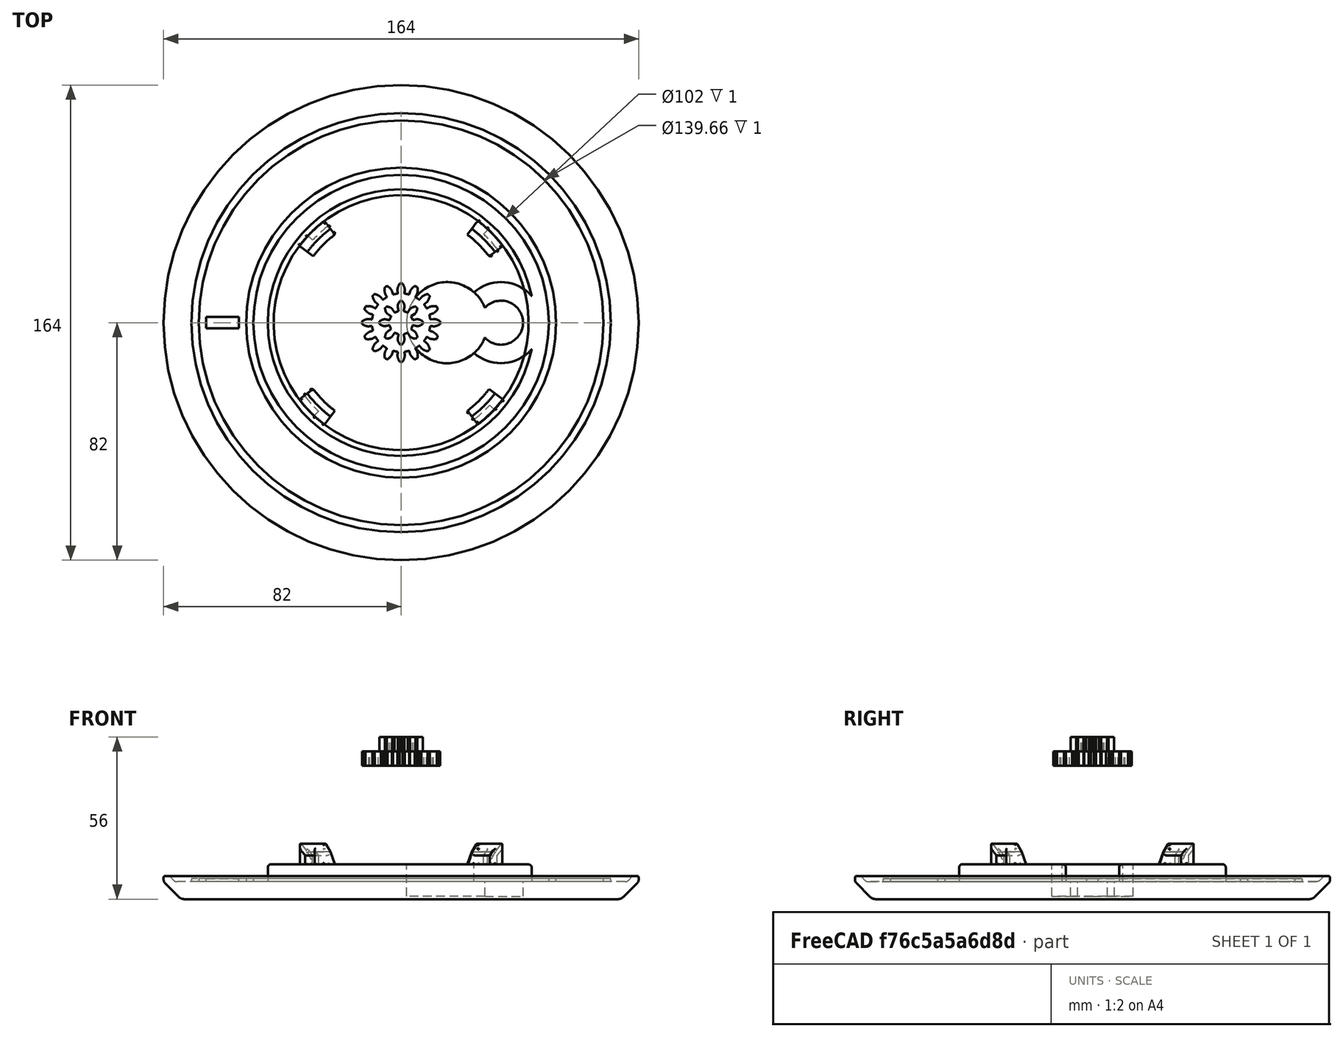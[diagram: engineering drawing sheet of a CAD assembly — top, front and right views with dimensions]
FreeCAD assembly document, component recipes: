
FREECAD ASSEMBLY — COMPONENT RECIPES ("smart_medication_box_v2")

This assembly document has 7 components, labeled P0..P6 below (a component is one placed body or linked part). 7 of them carry a construction recipe — the FreeCAD feature program that regenerates the part from scratch, quoted from this document or its linked companion documents; the rest are supplied as boundary geometry only. No exploded tour is included for this assembly.
COMPONENT P0 — recipe-attached ("base", modeled in this document).
Construction recipe (the document's own serialized feature program — sketch geometry with constraints, then the solid features built on it; lengths are millimeters unless a unit is written):

FEATURE [Sketcher::SketchObject] Sketch003
  ArcFitTolerance = 1e-06
  AttachmentSupport = -> [Origin006,XY_Plane003]
  FullyConstrained = true
  MakeInternals = true
  MapMode = 5
  expr: Constraints[0] = 104
  sketch-geometry (1):
    g0: Circle CenterX=0 CenterY=0 CenterZ=0 NormalX=0 NormalY=0 NormalZ=1 AngleXU=0 Radius=52
  constraints (2):
    c: Diameter(g0) = 104
    c: Coincident(g0,g-1)
FEATURE [PartDesign::Pad] Pad
  Direction = (0,0,1)
  Length = 6
  Length2 = 10
  Profile = -> Sketch003
  ReferenceAxis = -> Sketch003 [N_Axis]
  Refine = true
  Suppressed = false
  Type = 0
  expr: Length = 6
FEATURE [Sketcher::SketchObject] Sketch004
  ArcFitTolerance = 1e-06
  AttachmentSupport = -> [Pad]
  FullyConstrained = true
  MakeInternals = false
  MapMode = 5
  Placement = pos=(0,0,6) rot=(0,0,1;0rad)
  expr: Constraints[0] = 48 * 2 - 2
  sketch-geometry (1):
    g0: Circle CenterX=0 CenterY=0 CenterZ=0 NormalX=0 NormalY=0 NormalZ=1 AngleXU=0 Radius=47
  constraints (2):
    c: Diameter(g0) = 94
    c: Coincident(g0,g-1)
FEATURE [PartDesign::Pad] Pad001
  BaseFeature = -> Pad
  Direction = (0,0,1)
  Length = 6
  Length2 = 10
  Profile = -> Sketch004
  ReferenceAxis = -> Sketch004 [N_Axis]
  Refine = true
  Suppressed = false
  Type = 0
  expr: Length = 6
FEATURE [Sketcher::SketchObject] Sketch005
  ArcFitTolerance = 1e-06
  AttachmentSupport = -> [Pad001]
  ExternalGeometry = -> [Pad001]
  FullyConstrained = true
  MakeInternals = false
  MapMode = 5
  Placement = pos=(0,0,12) rot=(0,0,1;0rad)
  expr: Constraints[0] = 28
  expr: Constraints[4] = 11.5
  sketch-geometry (2):
    g0: Circle CenterX=35.5 CenterY=0 CenterZ=0 NormalX=0 NormalY=0 NormalZ=1 AngleXU=0 Radius=14
    g1: Circle [constr] CenterX=35.5 CenterY=0 CenterZ=0 NormalX=0 NormalY=0 NormalZ=1 AngleXU=0 Radius=11.5
  constraints (5):
    c: Diameter(g0) = 28
    c: Coincident(g1,g0)
    c: Tangent(g1,g-3)
    c: PointOnObject(g0,g-1)
    c: Distance(g0,g-3) = 11.5
FEATURE [PartDesign::Pocket] Pocket001
  BaseFeature = -> Pad001
  Direction = (0,0,-1)
  Length = 6
  Length2 = 5
  Profile = -> Sketch005
  ReferenceAxis = -> Sketch005 [N_Axis]
  Refine = true
  Suppressed = false
  Type = 0
  expr: Length = 6
FEATURE [Sketcher::SketchObject] Sketch006
  ArcFitTolerance = 1e-06
  AttachmentSupport = -> [Pocket001]
  ExternalGeometry = -> [Pocket001]
  FullyConstrained = true
  MakeInternals = false
  MapMode = 5
  Placement = pos=(0,0,6) rot=(0,0,1;0rad)
  sketch-geometry (1):
    g0: Circle CenterX=35.5 CenterY=0 CenterZ=0 NormalX=0 NormalY=0 NormalZ=1 AngleXU=0 Radius=7.6
  constraints (2):
    c: Diameter(g0) = 15.2
    c: Coincident(g0,g-4)
FEATURE [PartDesign::Pocket] Pocket002
  BaseFeature = -> Pocket001
  Direction = (0,0,-1)
  Length = 5
  Length2 = 5
  Profile = -> Sketch006
  ReferenceAxis = -> Sketch006 [N_Axis]
  Refine = true
  Suppressed = false
  Type = 0
FEATURE [Sketcher::SketchObject] Sketch007
  ArcFitTolerance = 1e-06
  AttachmentSupport = -> [Pocket002]
  ExternalGeometry = -> [Pocket002]
  FullyConstrained = true
  MakeInternals = false
  MapMode = 5
  Placement = pos=(0,0,12) rot=(0,0,1;0rad)
  expr: Constraints[0] = 28
  expr: Constraints[2] = -3
  sketch-geometry (1):
    g0: Circle CenterX=16.9 CenterY=0 CenterZ=0 NormalX=0 NormalY=0 NormalZ=1 AngleXU=0 Radius=14
  constraints (3):
    c: Diameter(g0) = 28
    c: PointOnObject(g0,g-1)
    c: Distance(g0,g-3) = -3
FEATURE [PartDesign::Pocket] Pocket003
  BaseFeature = -> Pocket002
  Direction = (0,0,-1)
  Length = 11
  Length2 = 5
  Profile = -> Sketch007
  ReferenceAxis = -> Sketch007 [N_Axis]
  Refine = true
  Suppressed = false
  Type = 0
  expr: Length = 11
FEATURE [Sketcher::SketchObject] Sketch009
  ArcFitTolerance = 1e-06
  FullyConstrained = true
  MakeInternals = false
  MapMode = 5
  Placement = pos=(53,0,0) rot=(1,0,0;1.5708rad)
  expr: Constraints[10] = 2
  expr: Constraints[3] = 22
  sketch-geometry (17):
    g0: LineSegment StartX=0 StartY=0 StartZ=0 EndX=0 EndY=3 EndZ=0
    g1: LineSegment StartX=0 StartY=3 StartZ=0 EndX=21.1716 EndY=3 EndZ=0
    g2: LineSegment StartX=22.5858 StartY=3.58579 StartZ=0 EndX=23.7071 EndY=4.70711 EndZ=0
    g3: LineSegment StartX=24.4142 StartY=5 StartZ=0 EndX=25.4142 EndY=5 EndZ=0
    g4: LineSegment StartX=26.4142 StartY=4 StartZ=0 EndX=26.4142 EndY=3.82843 EndZ=0
    g5: LineSegment StartX=25.8284 StartY=2.41421 StartZ=0 EndX=24 EndY=0.585786 EndZ=0
    g6: LineSegment StartX=0 StartY=0 StartZ=0 EndX=22.5858 EndY=0 EndZ=0
    g7: ArcOfCircle CenterX=25.4142 CenterY=4 CenterZ=0 NormalX=0 NormalY=0 NormalZ=1 AngleXU=0 Radius=1 StartAngle=0 EndAngle=1.5708
    g8: GeomPoint [constr] X=26.4142 Y=5 Z=0
    g9: ArcOfCircle CenterX=24.4142 CenterY=4 CenterZ=0 NormalX=0 NormalY=0 NormalZ=1 AngleXU=0 Radius=1 StartAngle=1.5708 EndAngle=2.35619
    g10: GeomPoint [constr] X=24 Y=5 Z=0
    g11: ArcOfCircle CenterX=24.4142 CenterY=3.82843 CenterZ=0 NormalX=0 NormalY=0 NormalZ=1 AngleXU=0 Radius=2 StartAngle=5.49779 EndAngle=6.28319
    g12: GeomPoint [constr] X=26.4142 Y=3 Z=0
    g13: ArcOfCircle CenterX=21.1716 CenterY=5 CenterZ=0 NormalX=0 NormalY=0 NormalZ=1 AngleXU=0 Radius=2 StartAngle=4.71239 EndAngle=5.49779
    g14: GeomPoint [constr] X=22 Y=3 Z=0
    g15: ArcOfCircle CenterX=22.5858 CenterY=2 CenterZ=0 NormalX=0 NormalY=0 NormalZ=1 AngleXU=0 Radius=2 StartAngle=4.71239 EndAngle=5.49779
    g16: GeomPoint [constr] X=23.4142 Y=0 Z=0
  constraints (40):
    c: Coincident(g-1,g0)
    c: Coincident(g0,g1)
    c: PointOnObject(g0,g-2)
    c: DistanceX(g1,g14) = 22
    c: PointOnObject(g16,g-1)
    c: Coincident(g6,g0)
    c: Parallel(g1,g6)
    c: Parallel(g3,g1)
    c: Perpendicular(g3,g4)
    c: PointOnObject(g12,g1)
    c: DistanceY(g12,g8) = 2
    c: PointOnObject(g8,g3)
    c: PointOnObject(g8,g4)
    c: Tangent(g3,g7) = 1.5708
    c: Tangent(g4,g7) = 1.5708
    c: PointOnObject(g10,g2)
    c: PointOnObject(g10,g3)
    c: Tangent(g2,g9) = 1.5708
    c: Tangent(g3,g9) = 1.5708
    c: PointOnObject(g12,g5)
    c: PointOnObject(g12,g4)
    c: Tangent(g5,g11) = 1.5708
    c: Tangent(g4,g11) = 1.5708
    c: PointOnObject(g14,g2)
    c: PointOnObject(g14,g1)
    c: Tangent(g2,g13) = -1.5708
    c: Tangent(g1,g13) = -1.5708
    c: PointOnObject(g16,g5)
    c: PointOnObject(g16,g6)
    c: Tangent(g5,g15) = 1.5708
    c: Tangent(g6,g15) = -1.5708
    c: Equal(g9,g7)
    c: Equal(g13,g11)
    c: Equal(g11,g15)
    c: Radius(g9) = 1
    c: Radius(g13) = 2
    c: Parallel(g5,g2)
    c: Angle(g-1,g5) = 0.785398
    c: DistanceY(g0,g0) = 3
    c: Distance(g3,g3) = 1
FEATURE [PartDesign::Revolution] Revolution
  Angle = 360
  Angle2 = 60
  Axis = (1e-16,1e-16,1)
  Base = (0,0,0)
  BaseFeature = -> Pocket003
  Profile = -> Sketch009
  ReferenceAxis = -> Z_Axis003
  Refine = true
  Reversed = true
  Suppressed = false
  Type = 0
FEATURE [PartDesign::Fillet] Fillet
  Base = -> Revolution [Edge30]
  BaseFeature = -> Revolution
  Radius = 1
  Refine = true
  SupportTransform = false
  Suppressed = false
  UseAllEdges = false
FEATURE [Sketcher::SketchObject] Sketch019
  ArcFitTolerance = 1e-06
  AttachmentSupport = -> [Fillet]
  FullyConstrained = true
  MakeInternals = false
  MapMode = 5
  Placement = pos=(0,0,12) rot=(0,0,1;0rad)
  sketch-geometry (1):
    g0: Circle CenterX=0 CenterY=0 CenterZ=0 NormalX=0 NormalY=0 NormalZ=1 AngleXU=0 Radius=44
  constraints (2):
    c: Diameter(g0) = 88
    c: Coincident(g0,g-1)
FEATURE [Sketcher::SketchObject] Sketch020
  ArcFitTolerance = 1e-06
  FullyConstrained = true
  MakeInternals = false
  MapMode = 5
  Placement = pos=(44,0,12) rot=(1,0,0;1.5708rad)
  sketch-geometry (9):
    g0: LineSegment StartX=-2.19203 StartY=0 StartZ=0 EndX=-2.19203 EndY=3.1 EndZ=0
    g1: LineSegment StartX=-2.19203 StartY=3.1 StartZ=0 EndX=0 EndY=5.29203 EndZ=0
    g2: LineSegment StartX=0 StartY=5.29203 StartZ=0 EndX=0 EndY=7.79203 EndZ=0
    g3: LineSegment StartX=-5.9535 StartY=0 StartZ=0 EndX=-2.19203 EndY=0 EndZ=0
    g4: LineSegment StartX=0 StartY=7.79203 StartZ=0 EndX=-3.44203 EndY=4.35 EndZ=0
    g5: LineSegment StartX=-3.44203 StartY=4.35 StartZ=0 EndX=-5.9535 EndY=0 EndZ=0
    g6: LineSegment [constr] StartX=-3.44203 StartY=4.35 StartZ=0 EndX=-2.19203 EndY=3.1 EndZ=0
    g7: LineSegment StartX=-2.19203 StartY=0 StartZ=0 EndX=0 EndY=0 EndZ=0
    g8: LineSegment StartX=0 StartY=0 StartZ=0 EndX=0 EndY=5.29203 EndZ=0
  constraints (24):
    c: PointOnObject(g0,g-1)
    c: Vertical(g0)
    c: Coincident(g0,g1)
    c: PointOnObject(g1,g-2)
    c: Coincident(g1,g2)
    c: Coincident(g3,g0)
    c: PointOnObject(g3,g-1)
    c: PointOnObject(g2,g-2)
    c: Angle(g1,g0) = 0.785398
    c: DistanceY(g0,g0) = 3.1
    c: Equal(g1,g0)
    c: DistanceY(g2,g2) = 2.5
    c: Coincident(g2,g4)
    c: Coincident(g4,g5)
    c: Coincident(g3,g5)
    c: Angle(g3,g5) = 1.0472
    c: Parallel(g4,g1)
    c: Coincident(g6,g4)
    c: Coincident(g6,g0)
    c: Perpendicular(g4,g6)
    c: Coincident(g7,g0)
    c: Coincident(g7,g-1)
    c: Coincident(g8,g7)
    c: Coincident(g8,g1)
FEATURE [PartDesign::Revolution] Revolution005
  Angle = 323
  Angle2 = 47
  Axis = (1e-16,1e-16,1)
  Base = (0,0,0)
  BaseFeature = -> Fillet
  Profile = -> Sketch020 [Edge4,Edge5,Edge2,Edge1,Edge3,Edge6]
  ReferenceAxis = -> Z_Axis003
  Refine = true
  Reversed = true
  Suppressed = false
  Type = 4
  expr: Angle = 323
  expr: Angle2 = 47
FEATURE [PartDesign::Revolution] Revolution006
  Angle = 313
  Angle2 = 53
  Axis = (1e-16,1e-16,1)
  Base = (0,0,0)
  BaseFeature = -> Revolution005
  Profile = -> Sketch020 [Edge8,Edge3,Edge4,Edge5,Edge6,Edge7]
  ReferenceAxis = -> Z_Axis003
  Refine = true
  Reversed = true
  Suppressed = false
  Type = 4
  expr: Angle = 313
  expr: Angle2 = 53
FEATURE [PartDesign::PolarPattern] PolarPattern004
  Angle = 360
  Axis = -> Z_Axis003
  BaseFeature = -> Revolution006
  Mode = 0
  Occurrences = 4
  Offset = 120
  Originals = -> [Revolution005,Revolution006]
  Refine = true
  Suppressed = false
  TransformMode = 0
  expr: Occurrences = 4
FEATURE [PartDesign::Fillet] Fillet005
  Base = -> PolarPattern004 [Face5]
  BaseFeature = -> PolarPattern004
  Radius = 0.5
  Refine = true
  SupportTransform = false
  Suppressed = false
  UseAllEdges = false
  expr: Radius = 0.5
FEATURE [PartDesign::Fillet] Fillet006
  Base = -> Fillet005 [?Face21,Face20]
  BaseFeature = -> Fillet005
  Radius = 0.5
  Refine = true
  SupportTransform = false
  Suppressed = false
  UseAllEdges = false
  expr: Radius = 0.5
FEATURE [PartDesign::Fillet] Fillet007
  Base = -> Fillet006 [Face29,Face32]
  BaseFeature = -> Fillet006
  Radius = 0.5
  Refine = true
  SupportTransform = false
  Suppressed = false
  UseAllEdges = false
FEATURE [PartDesign::Fillet] Fillet008
  Base = -> Fillet007 [Face44,Face41]
  BaseFeature = -> Fillet007
  Radius = 0.5
  Refine = true
  SupportTransform = false
  Suppressed = false
  UseAllEdges = false
FEATURE [Sketcher::SketchObject] Sketch027
  ArcFitTolerance = 1e-06
  AttachmentSupport = -> [Fillet008]
  ExternalGeometry = -> [Fillet008]
  FullyConstrained = true
  MakeInternals = false
  MapMode = 5
  Placement = pos=(7e-16,7e-16,6) rot=(0,0,1;0rad)
  expr: Constraints[7] = 1
  sketch-geometry (4):
    g0: Circle CenterX=0 CenterY=0 CenterZ=0 NormalX=0 NormalY=0 NormalZ=1 AngleXU=0 Radius=51
    g1: Circle CenterX=0 CenterY=0 CenterZ=0 NormalX=0 NormalY=0 NormalZ=1 AngleXU=0 Radius=76.3276
    g2: Circle CenterX=0 CenterY=0 CenterZ=0 NormalX=0 NormalY=0 NormalZ=1 AngleXU=0 Radius=73.8276
    g3: Circle CenterX=0 CenterY=0 CenterZ=0 NormalX=0 NormalY=0 NormalZ=1 AngleXU=0 Radius=68.8276
  constraints (11):
    c: PointOnObject(g0,g-1)
    c: PointOnObject(g0,g-2)
    c: Distance(g0,g-3) = 5
    c: PointOnObject(g1,g-1)
    c: PointOnObject(g2,g-1)
    c: PointOnObject(g2,g-2)
    c: PointOnObject(g1,g-2)
    c: Distance(g1,g-4) = 1
    c: Distance(g1,g2) = 2.5
    c: Coincident(g3,g0)
    c: Distance(g2,g3) = 5
FEATURE [PartDesign::Body] Body003
  AllowCompound = false
  Group = -> [Sketch003,Pad,Sketch004,Pad001,Sketch005,Pocket001,Sketch006,Pocket002,Sketch007,Pocket003,Sketch009,Revolution,Fillet,Sketch019,Sketch020,Revolution005,Revolution006,PolarPattern004,Fillet005,Fillet006,Fillet007,Fillet008,Sketch027]
  Origin = -> Origin006
  Tip = -> Fillet008
COMPONENT P1 — recipe-attached ("middle_gear", modeled in this document).
Construction recipe (the document's own serialized feature program — sketch geometry with constraints, then the solid features built on it; lengths are millimeters unless a unit is written):

FEATURE [PartDesign::Boolean] Boolean
  Group = -> [InvoluteGear003,InvoluteGear002,Body017]
  Refine = true
  Suppressed = false
  Type = 0
  UsePlacement = true
FEATURE [PartDesign::Fillet] Fillet001
  Base = -> Boolean [Face4]
  BaseFeature = -> Boolean
  Radius = 0.25
  Refine = true
  SupportTransform = false
  Suppressed = false
  UseAllEdges = false
  expr: Radius = 0.25
FEATURE [PartDesign::Fillet] Fillet002
  Base = -> Fillet001 [Face4,Face243]
  BaseFeature = -> Fillet001
  Radius = 0.2
  Refine = true
  SupportTransform = false
  Suppressed = false
  UseAllEdges = false
  expr: Radius = 0.2
FEATURE [PartDesign::Body] Body018
  AllowCompound = false
  Group = -> [Boolean,Fillet001,Fillet002]
  Origin = -> Origin030
  Tip = -> Fillet002
COMPONENT P2 — recipe-attached ("cover", modeled in this document).
Construction recipe (the document's own serialized feature program — sketch geometry with constraints, then the solid features built on it; lengths are millimeters unless a unit is written):

FEATURE [Sketcher::SketchObject] Sketch024
  ArcFitTolerance = 1e-06
  AttachmentSupport = -> [Origin040]
  FullyConstrained = true
  MakeInternals = false
  MapMode = 5
  sketch-geometry (5):
    g0: ArcOfCircle CenterX=0 CenterY=0 CenterZ=0 NormalX=0 NormalY=0 NormalZ=1 AngleXU=0 Radius=100 StartAngle=4.71239 EndAngle=10.7992
    g1: ArcOfCircle CenterX=0 CenterY=0 CenterZ=0 NormalX=0 NormalY=0 NormalZ=1 AngleXU=0 Radius=41 StartAngle=4.51604 EndAngle=4.71239
    g2: Circle CenterX=0 CenterY=0 CenterZ=0 NormalX=0 NormalY=0 NormalZ=1 AngleXU=0 Radius=38
    g3: LineSegment StartX=-7.5e-15 StartY=-41 StartZ=0 EndX=-1.84e-14 EndY=-100 EndZ=0
    g4: LineSegment StartX=-19.509 StartY=-98.0785 StartZ=0 EndX=-7.99869 EndY=-40.2122 EndZ=0
  constraints (14):
    c: Angle(g0) = 6.08684
    c: Coincident(g0,g-1)
    c: PointOnObject(g0,g-2)
    c: Coincident(g1,g0)
    c: PointOnObject(g1,g-2)
    c: Diameter(g2) = 76
    c: Coincident(g2,g0)
    c: Radius(g0) = 100
    c: Distance(g1,g2) = 3
    c: Coincident(g3,g1)
    c: Coincident(g3,g0)
    c: Coincident(g4,g0)
    c: Coincident(g4,g1)
    c: PointOnObject(g0,g4)
FEATURE [PartDesign::Pad] Pad008
  Direction = (0,0,1)
  Length = 1.5
  Length2 = 10
  Profile = -> Sketch024
  ReferenceAxis = -> Sketch024 [N_Axis]
  Refine = true
  Suppressed = false
  Type = 0
  expr: Length = 1.5
FEATURE [Sketcher::SketchObject] Sketch025
  ArcFitTolerance = 1e-06
  ExternalGeometry = -> [Pad008]
  FullyConstrained = false
  MakeInternals = false
  MapMode = 5
  Placement = pos=(-1.84e-14,-100,0) rot=(0.57735,-0.57735,-0.57735;2.0944rad)
  sketch-geometry (10):
    g0: LineSegment StartX=0 StartY=0 StartZ=0 EndX=0.693802 EndY=-1.2017 EndZ=0
    g1: LineSegment StartX=1.21047 StartY=-1.5 StartZ=0 EndX=2.01139 EndY=-1.5 EndZ=0
    g2: LineSegment StartX=2.37172 StartY=-0.875891 StartZ=0 EndX=1.18232 EndY=1.18422 EndZ=0
    g3: LineSegment StartX=0.63537 StartY=1.5 StartZ=0 EndX=0 EndY=1.5 EndZ=0
    g4: ArcOfCircle CenterX=0.63537 CenterY=0.868442 CenterZ=0 NormalX=0 NormalY=0 NormalZ=1 AngleXU=0 Radius=0.631558 StartAngle=0.523599 EndAngle=1.5708
    g5: GeomPoint [constr] X=1 Y=1.5 Z=0
    g6: ArcOfCircle CenterX=2.01139 CenterY=-1.08393 CenterZ=0 NormalX=0 NormalY=0 NormalZ=1 AngleXU=0 Radius=0.416073 StartAngle=4.71239 EndAngle=6.80678
    g7: GeomPoint [constr] X=2.73205 Y=-1.5 Z=0
    g8: ArcOfCircle CenterX=1.21047 CenterY=-0.903401 CenterZ=0 NormalX=0 NormalY=0 NormalZ=1 AngleXU=0 Radius=0.596599 StartAngle=3.66519 EndAngle=4.71239
    g9: GeomPoint [constr] X=0.866025 Y=-1.5 Z=0
  constraints (20):
    c: Coincident(g-3,g0)
    c: Coincident(g3,g-3)
    c: Horizontal(g3)
    c: Parallel(g0,g2)
    c: Parallel(g1,g3)
    c: Angle(g-2,g0) = 0.523599
    c: Distance(g5,g1) = 3
    c: DistanceX(g3,g5) = 1
    c: PointOnObject(g5,g3)
    c: PointOnObject(g5,g2)
    c: Tangent(g3,g4) = -1.5708
    c: Tangent(g2,g4) = -1.5708
    c: PointOnObject(g7,g2)
    c: PointOnObject(g7,g1)
    c: Tangent(g2,g6) = -1.5708
    c: Tangent(g1,g6) = -1.5708
    c: PointOnObject(g9,g1)
    c: PointOnObject(g9,g0)
    c: Tangent(g1,g8) = -1.5708
    c: Tangent(g0,g8) = -1.5708
FEATURE [PartDesign::Revolution] Revolution007
  Angle = 360
  Angle2 = 348.75
  Axis = (0,0,1)
  Base = (0,0,0)
  BaseFeature = -> Pad008
  Profile = -> Sketch025
  ReferenceAxis = -> Pad008 [Edge3]
  Refine = true
  Reversed = true
  Suppressed = false
  Type = 4
FEATURE [Sketcher::SketchObject] Sketch026
  ArcFitTolerance = 1e-06
  AttachmentSupport = -> [Revolution007]
  ExternalGeometry = -> [Revolution007]
  FullyConstrained = true
  MakeInternals = false
  MapMode = 5
  Placement = pos=(0,0,0) rot=(1,0,0;3.14159rad)
  sketch-geometry (1):
    g0: Circle CenterX=0 CenterY=0 CenterZ=0 NormalX=0 NormalY=0 NormalZ=1 AngleXU=0 Radius=41
  constraints (2):
    c: Coincident(g0,g-3)
    c: PointOnObject(g-4,g0)
FEATURE [PartDesign::Pad] Pad009
  BaseFeature = -> Revolution007
  Direction = (0,0,-1)
  Length = 3
  Length2 = 10
  Profile = -> Sketch026
  ReferenceAxis = -> Sketch026 [N_Axis]
  Refine = true
  Suppressed = false
  Type = 0
  expr: Length = 3
FEATURE [PartDesign::Chamfer] Chamfer001
  Angle = 45
  Base = -> Pad009 [Edge34]
  BaseFeature = -> Pad009
  ChamferType = 0
  FlipDirection = false
  Refine = true
  Size = 2
  Size2 = 1
  SupportTransform = false
  Suppressed = false
  UseAllEdges = false
  expr: Size = 2
FEATURE [PartDesign::Fillet] Fillet013
  Base = -> Chamfer001 [Edge1,Edge2,Edge24,Edge19]
  BaseFeature = -> Chamfer001
  Radius = 0.5
  Refine = true
  SupportTransform = false
  Suppressed = false
  UseAllEdges = false
  expr: Radius = 0.5
FEATURE [PartDesign::Body] Body023  label="cover"
  AllowCompound = false
  Group = -> [Sketch024,Pad008,Sketch025,Revolution007,Sketch026,Pad009,Chamfer001,Fillet013]
  Origin = -> Origin040
  Placement = pos=(-3.2e-15,-3.5e-15,43) rot=(0,0,-1;6.08242rad)
  Tip = -> Fillet013
COMPONENT P3 — recipe-attached ("desc_upper_ring", modeled in this document).
Construction recipe (the document's own serialized feature program — sketch geometry with constraints, then the solid features built on it; lengths are millimeters unless a unit is written):

FEATURE [Sketcher::SketchObject] Sketch021
  ArcFitTolerance = 1e-06
  AttachmentSupport = -> [Origin036]
  FullyConstrained = true
  MakeInternals = false
  MapMode = 5
  expr: Constraints[2] = 42.75 * 2
  expr: Constraints[3] = 51 * 2
  sketch-geometry (2):
    g0: Circle CenterX=0 CenterY=0 CenterZ=0 NormalX=0 NormalY=0 NormalZ=1 AngleXU=0 Radius=42.75
    g1: Circle CenterX=0 CenterY=0 CenterZ=0 NormalX=0 NormalY=0 NormalZ=1 AngleXU=0 Radius=51
  constraints (4):
    c: Coincident(g0,g-1)
    c: Coincident(g1,g0)
    c: Diameter(g0) = 85.5
    c: Diameter(g1) = 102
FEATURE [PartDesign::Pad] Pad006
  Direction = (0,0,1)
  Length = 3
  Length2 = 10
  Profile = -> Sketch021
  ReferenceAxis = -> Sketch021 [N_Axis]
  Refine = true
  Suppressed = false
  Type = 0
  expr: Length = 3
FEATURE [Sketcher::SketchObject] Sketch022
  ArcFitTolerance = 1e-06
  AttachmentSupport = -> [Pad006]
  FullyConstrained = false
  MakeInternals = false
  MapMode = 5
  Placement = pos=(0,0,3) rot=(0,0,1;0rad)
  sketch-geometry (4):
    g0: ArcOfCircle CenterX=0 CenterY=0 CenterZ=0 NormalX=0 NormalY=0 NormalZ=1 AngleXU=0 Radius=44.08 StartAngle=1.00282 EndAngle=1.41716
    g1: ArcOfCircle CenterX=0 CenterY=0 CenterZ=0 NormalX=0 NormalY=0 NormalZ=1 AngleXU=0 Radius=50.08 StartAngle=1.00282 EndAngle=1.41716
    g2: LineSegment StartX=6.74568 StartY=43.5608 StartZ=0 EndX=7.66388 EndY=49.4901 EndZ=0
    g3: LineSegment StartX=23.7119 StartY=37.159 StartZ=0 EndX=26.9394 EndY=42.217 EndZ=0
  constraints (11):
    c: Coincident(g1,g0)
    c: Coincident(g2,g0)
    c: Coincident(g2,g1)
    c: Coincident(g3,g0)
    c: Coincident(g3,g1)
    c: Equal(g2,g3)
    c: Perpendicular(g0,g2)
    c: Distance(g3,g3) = 6
    c: Radius(g0) = 44.08
    c: Angle(g0) = 0.414341
    c: Coincident(g0,g-1)
FEATURE [PartDesign::Pocket] Pocket006
  BaseFeature = -> Pad006
  Direction = (0,0,-1)
  Length = 1.5
  Length2 = 5
  Profile = -> Sketch022
  ReferenceAxis = -> Sketch022 [N_Axis]
  Refine = true
  Suppressed = false
  Type = 0
  expr: Length = 1.5
FEATURE [PartDesign::PolarPattern] PolarPattern005
  Angle = 360
  Axis = -> Sketch022 [N_Axis]
  BaseFeature = -> Pocket006
  Mode = 0
  Occurrences = 2
  Offset = 120
  Originals = -> [Pocket006]
  Refine = true
  Suppressed = false
  TransformMode = 0
FEATURE [PartDesign::Fillet] Fillet010
  Base = -> PolarPattern005 [Face2]
  BaseFeature = -> PolarPattern005
  Radius = 0.3
  Refine = true
  SupportTransform = false
  Suppressed = false
  UseAllEdges = false
  expr: Radius = 0.3
FEATURE [PartDesign::Fillet] Fillet011
  Base = -> Fillet010 [Face3]
  BaseFeature = -> Fillet010
  Radius = 0.4
  Refine = true
  SupportTransform = false
  Suppressed = false
  UseAllEdges = false
  expr: Radius = 0.4
FEATURE [Sketcher::SketchObject] Sketch023
  ArcFitTolerance = 1e-06
  AttachmentSupport = -> [Fillet011]
  FullyConstrained = false
  MakeInternals = false
  MapMode = 5
  Placement = pos=(0,0,0) rot=(1,0,0;3.14159rad)
  sketch-geometry (1190):
    g0: BSplineCurve PolesCount=2 KnotsCount=2 Degree=1 IsPeriodic=0
    g1: BSplineCurve PolesCount=2 KnotsCount=2 Degree=1 IsPeriodic=0
    g2: BSplineCurve PolesCount=2 KnotsCount=2 Degree=1 IsPeriodic=0
    g3: BSplineCurve PolesCount=2 KnotsCount=2 Degree=1 IsPeriodic=0
    g4: BSplineCurve PolesCount=2 KnotsCount=2 Degree=1 IsPeriodic=0
    g5: BSplineCurve PolesCount=2 KnotsCount=2 Degree=1 IsPeriodic=0
    g6: BSplineCurve PolesCount=2 KnotsCount=2 Degree=1 IsPeriodic=0
    g7: BSplineCurve PolesCount=2 KnotsCount=2 Degree=1 IsPeriodic=0
    g8: BSplineCurve PolesCount=2 KnotsCount=2 Degree=1 IsPeriodic=0
    g9: BSplineCurve PolesCount=2 KnotsCount=2 Degree=1 IsPeriodic=0
    g10: BSplineCurve PolesCount=2 KnotsCount=2 Degree=1 IsPeriodic=0
    g11: BSplineCurve PolesCount=2 KnotsCount=2 Degree=1 IsPeriodic=0
    g12: BSplineCurve PolesCount=2 KnotsCount=2 Degree=1 IsPeriodic=0
    g13: BSplineCurve PolesCount=2 KnotsCount=2 Degree=1 IsPeriodic=0
    g14: BSplineCurve PolesCount=2 KnotsCount=2 Degree=1 IsPeriodic=0
    g15: BSplineCurve PolesCount=2 KnotsCount=2 Degree=1 IsPeriodic=0
    g16: BSplineCurve PolesCount=2 KnotsCount=2 Degree=1 IsPeriodic=0
    g17: BSplineCurve PolesCount=2 KnotsCount=2 Degree=1 IsPeriodic=0
    g18: BSplineCurve PolesCount=2 KnotsCount=2 Degree=1 IsPeriodic=0
    g19: BSplineCurve PolesCount=2 KnotsCount=2 Degree=1 IsPeriodic=0
    g20: BSplineCurve PolesCount=2 KnotsCount=2 Degree=1 IsPeriodic=0
    g21: BSplineCurve PolesCount=2 KnotsCount=2 Degree=1 IsPeriodic=0
    g22: BSplineCurve PolesCount=2 KnotsCount=2 Degree=1 IsPeriodic=0
    g23: BSplineCurve PolesCount=2 KnotsCount=2 Degree=1 IsPeriodic=0
    g24: BSplineCurve PolesCount=2 KnotsCount=2 Degree=1 IsPeriodic=0
    g25: BSplineCurve PolesCount=2 KnotsCount=2 Degree=1 IsPeriodic=0
    g26: BSplineCurve PolesCount=2 KnotsCount=2 Degree=1 IsPeriodic=0
    g27: BSplineCurve PolesCount=2 KnotsCount=2 Degree=1 IsPeriodic=0
    g28: BSplineCurve PolesCount=2 KnotsCount=2 Degree=1 IsPeriodic=0
    g29: BSplineCurve PolesCount=2 KnotsCount=2 Degree=1 IsPeriodic=0
    g30: BSplineCurve PolesCount=2 KnotsCount=2 Degree=1 IsPeriodic=0
    g31: BSplineCurve PolesCount=2 KnotsCount=2 Degree=1 IsPeriodic=0
    g32: BSplineCurve PolesCount=2 KnotsCount=2 Degree=1 IsPeriodic=0
    g33: BSplineCurve PolesCount=2 KnotsCount=2 Degree=1 IsPeriodic=0
    g34: BSplineCurve PolesCount=2 KnotsCount=2 Degree=1 IsPeriodic=0
    g35: BSplineCurve PolesCount=2 KnotsCount=2 Degree=1 IsPeriodic=0
    g36: BSplineCurve PolesCount=2 KnotsCount=2 Degree=1 IsPeriodic=0
    g37: BSplineCurve PolesCount=2 KnotsCount=2 Degree=1 IsPeriodic=0
    g38: BSplineCurve PolesCount=2 KnotsCount=2 Degree=1 IsPeriodic=0
    g39: BSplineCurve PolesCount=2 KnotsCount=2 Degree=1 IsPeriodic=0
    g40: BSplineCurve PolesCount=2 KnotsCount=2 Degree=1 IsPeriodic=0
    g41: BSplineCurve PolesCount=2 KnotsCount=2 Degree=1 IsPeriodic=0
    g42: BSplineCurve PolesCount=2 KnotsCount=2 Degree=1 IsPeriodic=0
    g43: BSplineCurve PolesCount=2 KnotsCount=2 Degree=1 IsPeriodic=0
    g44: BSplineCurve PolesCount=2 KnotsCount=2 Degree=1 IsPeriodic=0
    g45: BSplineCurve PolesCount=2 KnotsCount=2 Degree=1 IsPeriodic=0
    g46: BSplineCurve PolesCount=2 KnotsCount=2 Degree=1 IsPeriodic=0
    g47: BSplineCurve PolesCount=2 KnotsCount=2 Degree=1 IsPeriodic=0
    g48: BSplineCurve PolesCount=2 KnotsCount=2 Degree=1 IsPeriodic=0
    g49: BSplineCurve PolesCount=2 KnotsCount=2 Degree=1 IsPeriodic=0
    g50: BSplineCurve PolesCount=2 KnotsCount=2 Degree=1 IsPeriodic=0
    g51: BSplineCurve PolesCount=2 KnotsCount=2 Degree=1 IsPeriodic=0
    g52: BSplineCurve PolesCount=2 KnotsCount=2 Degree=1 IsPeriodic=0
    g53: BSplineCurve PolesCount=2 KnotsCount=2 Degree=1 IsPeriodic=0
    g54: BSplineCurve PolesCount=2 KnotsCount=2 Degree=1 IsPeriodic=0
    g55: BSplineCurve PolesCount=2 KnotsCount=2 Degree=1 IsPeriodic=0
    g56: BSplineCurve PolesCount=2 KnotsCount=2 Degree=1 IsPeriodic=0
    g57: BSplineCurve PolesCount=2 KnotsCount=2 Degree=1 IsPeriodic=0
    g58: BSplineCurve PolesCount=2 KnotsCount=2 Degree=1 IsPeriodic=0
    g59: BSplineCurve PolesCount=2 KnotsCount=2 Degree=1 IsPeriodic=0
    g60: BSplineCurve PolesCount=2 KnotsCount=2 Degree=1 IsPeriodic=0
    g61: BSplineCurve PolesCount=2 KnotsCount=2 Degree=1 IsPeriodic=0
    g62: BSplineCurve PolesCount=2 KnotsCount=2 Degree=1 IsPeriodic=0
    g63: BSplineCurve PolesCount=2 KnotsCount=2 Degree=1 IsPeriodic=0
    g64: BSplineCurve PolesCount=2 KnotsCount=2 Degree=1 IsPeriodic=0
    g65: BSplineCurve PolesCount=2 KnotsCount=2 Degree=1 IsPeriodic=0
    g66: BSplineCurve PolesCount=2 KnotsCount=2 Degree=1 IsPeriodic=0
    g67: BSplineCurve PolesCount=2 KnotsCount=2 Degree=1 IsPeriodic=0
    g68: BSplineCurve PolesCount=2 KnotsCount=2 Degree=1 IsPeriodic=0
    g69: BSplineCurve PolesCount=2 KnotsCount=2 Degree=1 IsPeriodic=0
    g70: BSplineCurve PolesCount=2 KnotsCount=2 Degree=1 IsPeriodic=0
    g71: BSplineCurve PolesCount=2 KnotsCount=2 Degree=1 IsPeriodic=0
    g72: BSplineCurve PolesCount=2 KnotsCount=2 Degree=1 IsPeriodic=0
    g73: BSplineCurve PolesCount=2 KnotsCount=2 Degree=1 IsPeriodic=0
    g74: BSplineCurve PolesCount=2 KnotsCount=2 Degree=1 IsPeriodic=0
    g75: BSplineCurve PolesCount=2 KnotsCount=2 Degree=1 IsPeriodic=0
    g76: BSplineCurve PolesCount=2 KnotsCount=2 Degree=1 IsPeriodic=0
    g77: BSplineCurve PolesCount=2 KnotsCount=2 Degree=1 IsPeriodic=0
    g78: BSplineCurve PolesCount=2 KnotsCount=2 Degree=1 IsPeriodic=0
    g79: BSplineCurve PolesCount=2 KnotsCount=2 Degree=1 IsPeriodic=0
    g80: BSplineCurve PolesCount=2 KnotsCount=2 Degree=1 IsPeriodic=0
    g81: BSplineCurve PolesCount=2 KnotsCount=2 Degree=1 IsPeriodic=0
    g82: BSplineCurve PolesCount=2 KnotsCount=2 Degree=1 IsPeriodic=0
    g83: BSplineCurve PolesCount=2 KnotsCount=2 Degree=1 IsPeriodic=0
    g84: BSplineCurve PolesCount=2 KnotsCount=2 Degree=1 IsPeriodic=0
    g85: BSplineCurve PolesCount=2 KnotsCount=2 Degree=1 IsPeriodic=0
    g86: BSplineCurve PolesCount=2 KnotsCount=2 Degree=1 IsPeriodic=0
    g87: BSplineCurve PolesCount=2 KnotsCount=2 Degree=1 IsPeriodic=0
    g88: BSplineCurve PolesCount=2 KnotsCount=2 Degree=1 IsPeriodic=0
    g89: BSplineCurve PolesCount=2 KnotsCount=2 Degree=1 IsPeriodic=0
    g90: BSplineCurve PolesCount=2 KnotsCount=2 Degree=1 IsPeriodic=0
    g91: BSplineCurve PolesCount=2 KnotsCount=2 Degree=1 IsPeriodic=0
    g92: BSplineCurve PolesCount=2 KnotsCount=2 Degree=1 IsPeriodic=0
    g93: BSplineCurve PolesCount=2 KnotsCount=2 Degree=1 IsPeriodic=0
    g94: BSplineCurve PolesCount=2 KnotsCount=2 Degree=1 IsPeriodic=0
    g95: BSplineCurve PolesCount=2 KnotsCount=2 Degree=1 IsPeriodic=0
    g96: BSplineCurve PolesCount=2 KnotsCount=2 Degree=1 IsPeriodic=0
    g97: BSplineCurve PolesCount=2 KnotsCount=2 Degree=1 IsPeriodic=0
    g98: BSplineCurve PolesCount=2 KnotsCount=2 Degree=1 IsPeriodic=0
    g99: BSplineCurve PolesCount=2 KnotsCount=2 Degree=1 IsPeriodic=0
    g100: BSplineCurve PolesCount=2 KnotsCount=2 Degree=1 IsPeriodic=0
    g101: BSplineCurve PolesCount=2 KnotsCount=2 Degree=1 IsPeriodic=0
    g102: BSplineCurve PolesCount=2 KnotsCount=2 Degree=1 IsPeriodic=0
    g103: BSplineCurve PolesCount=2 KnotsCount=2 Degree=1 IsPeriodic=0
    g104: BSplineCurve PolesCount=2 KnotsCount=2 Degree=1 IsPeriodic=0
    g105: BSplineCurve PolesCount=2 KnotsCount=2 Degree=1 IsPeriodic=0
    g106: BSplineCurve PolesCount=2 KnotsCount=2 Degree=1 IsPeriodic=0
    g107: BSplineCurve PolesCount=2 KnotsCount=2 Degree=1 IsPeriodic=0
    g108: BSplineCurve PolesCount=2 KnotsCount=2 Degree=1 IsPeriodic=0
    g109: BSplineCurve PolesCount=2 KnotsCount=2 Degree=1 IsPeriodic=0
    g110: BSplineCurve PolesCount=2 KnotsCount=2 Degree=1 IsPeriodic=0
    g111: BSplineCurve PolesCount=2 KnotsCount=2 Degree=1 IsPeriodic=0
    g112: BSplineCurve PolesCount=2 KnotsCount=2 Degree=1 IsPeriodic=0
    g113: BSplineCurve PolesCount=2 KnotsCount=2 Degree=1 IsPeriodic=0
    g114: BSplineCurve PolesCount=2 KnotsCount=2 Degree=1 IsPeriodic=0
    g115: BSplineCurve PolesCount=2 KnotsCount=2 Degree=1 IsPeriodic=0
    g116: BSplineCurve PolesCount=2 KnotsCount=2 Degree=1 IsPeriodic=0
    g117: BSplineCurve PolesCount=2 KnotsCount=2 Degree=1 IsPeriodic=0
    g118: BSplineCurve PolesCount=2 KnotsCount=2 Degree=1 IsPeriodic=0
    g119: BSplineCurve PolesCount=2 KnotsCount=2 Degree=1 IsPeriodic=0
    g120: BSplineCurve PolesCount=2 KnotsCount=2 Degree=1 IsPeriodic=0
    g121: BSplineCurve PolesCount=2 KnotsCount=2 Degree=1 IsPeriodic=0
    g122: BSplineCurve PolesCount=2 KnotsCount=2 Degree=1 IsPeriodic=0
    g123: BSplineCurve PolesCount=2 KnotsCount=2 Degree=1 IsPeriodic=0
    g124: BSplineCurve PolesCount=2 KnotsCount=2 Degree=1 IsPeriodic=0
    g125: BSplineCurve PolesCount=2 KnotsCount=2 Degree=1 IsPeriodic=0
    g126: BSplineCurve PolesCount=2 KnotsCount=2 Degree=1 IsPeriodic=0
    g127: BSplineCurve PolesCount=2 KnotsCount=2 Degree=1 IsPeriodic=0
    g128: BSplineCurve PolesCount=3 KnotsCount=2 Degree=2 IsPeriodic=0
    g129: BSplineCurve PolesCount=3 KnotsCount=2 Degree=2 IsPeriodic=0
    g130: BSplineCurve PolesCount=3 KnotsCount=2 Degree=2 IsPeriodic=0
    g131: BSplineCurve PolesCount=3 KnotsCount=2 Degree=2 IsPeriodic=0
    g132: BSplineCurve PolesCount=3 KnotsCount=2 Degree=2 IsPeriodic=0
    g133: BSplineCurve PolesCount=3 KnotsCount=2 Degree=2 IsPeriodic=0
    g134: BSplineCurve PolesCount=3 KnotsCount=2 Degree=2 IsPeriodic=0
    g135: BSplineCurve PolesCount=3 KnotsCount=2 Degree=2 IsPeriodic=0
    g136: BSplineCurve PolesCount=3 KnotsCount=2 Degree=2 IsPeriodic=0
    g137: BSplineCurve PolesCount=3 KnotsCount=2 Degree=2 IsPeriodic=0
    g138: BSplineCurve PolesCount=3 KnotsCount=2 Degree=2 IsPeriodic=0
    g139: BSplineCurve PolesCount=3 KnotsCount=2 Degree=2 IsPeriodic=0
    g140: BSplineCurve PolesCount=3 KnotsCount=2 Degree=2 IsPeriodic=0
    g141: BSplineCurve PolesCount=3 KnotsCount=2 Degree=2 IsPeriodic=0
    g142: BSplineCurve PolesCount=3 KnotsCount=2 Degree=2 IsPeriodic=0
    g143: BSplineCurve PolesCount=3 KnotsCount=2 Degree=2 IsPeriodic=0
    g144: BSplineCurve PolesCount=2 KnotsCount=2 Degree=1 IsPeriodic=0
    g145: BSplineCurve PolesCount=2 KnotsCount=2 Degree=1 IsPeriodic=0
    g146: BSplineCurve PolesCount=2 KnotsCount=2 Degree=1 IsPeriodic=0
    g147: BSplineCurve PolesCount=2 KnotsCount=2 Degree=1 IsPeriodic=0
    g148: BSplineCurve PolesCount=2 KnotsCount=2 Degree=1 IsPeriodic=0
    g149: BSplineCurve PolesCount=2 KnotsCount=2 Degree=1 IsPeriodic=0
    g150: BSplineCurve PolesCount=2 KnotsCount=2 Degree=1 IsPeriodic=0
    g151: BSplineCurve PolesCount=2 KnotsCount=2 Degree=1 IsPeriodic=0
    g152: BSplineCurve PolesCount=2 KnotsCount=2 Degree=1 IsPeriodic=0
    g153: BSplineCurve PolesCount=2 KnotsCount=2 Degree=1 IsPeriodic=0
    g154: BSplineCurve PolesCount=2 KnotsCount=2 Degree=1 IsPeriodic=0
    g155: BSplineCurve PolesCount=2 KnotsCount=2 Degree=1 IsPeriodic=0
    g156: BSplineCurve PolesCount=3 KnotsCount=2 Degree=2 IsPeriodic=0
    g157: BSplineCurve PolesCount=3 KnotsCount=2 Degree=2 IsPeriodic=0
    g158: BSplineCurve PolesCount=3 KnotsCount=2 Degree=2 IsPeriodic=0
    g159: BSplineCurve PolesCount=3 KnotsCount=2 Degree=2 IsPeriodic=0
    g160: BSplineCurve PolesCount=3 KnotsCount=2 Degree=2 IsPeriodic=0
    g161: BSplineCurve PolesCount=3 KnotsCount=2 Degree=2 IsPeriodic=0
    g162: BSplineCurve PolesCount=3 KnotsCount=2 Degree=2 IsPeriodic=0
    g163: BSplineCurve PolesCount=3 KnotsCount=2 Degree=2 IsPeriodic=0
    g164: BSplineCurve PolesCount=3 KnotsCount=2 Degree=2 IsPeriodic=0
    g165: BSplineCurve PolesCount=3 KnotsCount=2 Degree=2 IsPeriodic=0
    g166: BSplineCurve PolesCount=2 KnotsCount=2 Degree=1 IsPeriodic=0
    g167: BSplineCurve PolesCount=3 KnotsCount=2 Degree=2 IsPeriodic=0
    g168: BSplineCurve PolesCount=3 KnotsCount=2 Degree=2 IsPeriodic=0
    g169: BSplineCurve PolesCount=3 KnotsCount=2 Degree=2 IsPeriodic=0
    g170: BSplineCurve PolesCount=3 KnotsCount=2 Degree=2 IsPeriodic=0
    g171: BSplineCurve PolesCount=3 KnotsCount=2 Degree=2 IsPeriodic=0
    g172: BSplineCurve PolesCount=3 KnotsCount=2 Degree=2 IsPeriodic=0
    g173: BSplineCurve PolesCount=3 KnotsCount=2 Degree=2 IsPeriodic=0
    g174: BSplineCurve PolesCount=3 KnotsCount=2 Degree=2 IsPeriodic=0
    g175: BSplineCurve PolesCount=3 KnotsCount=2 Degree=2 IsPeriodic=0
    g176: BSplineCurve PolesCount=2 KnotsCount=2 Degree=1 IsPeriodic=0
    g177: BSplineCurve PolesCount=2 KnotsCount=2 Degree=1 IsPeriodic=0
    g178: BSplineCurve PolesCount=2 KnotsCount=2 Degree=1 IsPeriodic=0
    g179: BSplineCurve PolesCount=3 KnotsCount=2 Degree=2 IsPeriodic=0
    g180: BSplineCurve PolesCount=3 KnotsCount=2 Degree=2 IsPeriodic=0
    g181: BSplineCurve PolesCount=3 KnotsCount=2 Degree=2 IsPeriodic=0
    g182: BSplineCurve PolesCount=3 KnotsCount=2 Degree=2 IsPeriodic=0
    g183: BSplineCurve PolesCount=2 KnotsCount=2 Degree=1 IsPeriodic=0
    g184: BSplineCurve PolesCount=3 KnotsCount=2 Degree=2 IsPeriodic=0
    g185: BSplineCurve PolesCount=3 KnotsCount=2 Degree=2 IsPeriodic=0
    g186: BSplineCurve PolesCount=3 KnotsCount=2 Degree=2 IsPeriodic=0
    g187: BSplineCurve PolesCount=3 KnotsCount=2 Degree=2 IsPeriodic=0
    g188: BSplineCurve PolesCount=3 KnotsCount=2 Degree=2 IsPeriodic=0
    g189: BSplineCurve PolesCount=2 KnotsCount=2 Degree=1 IsPeriodic=0
    g190: BSplineCurve PolesCount=2 KnotsCount=2 Degree=1 IsPeriodic=0
    g191: BSplineCurve PolesCount=2 KnotsCount=2 Degree=1 IsPeriodic=0
    g192: BSplineCurve PolesCount=3 KnotsCount=2 Degree=2 IsPeriodic=0
    g193: BSplineCurve PolesCount=3 KnotsCount=2 Degree=2 IsPeriodic=0
    g194: BSplineCurve PolesCount=3 KnotsCount=2 Degree=2 IsPeriodic=0
    g195: BSplineCurve PolesCount=3 KnotsCount=2 Degree=2 IsPeriodic=0
    g196: BSplineCurve PolesCount=3 KnotsCount=2 Degree=2 IsPeriodic=0
    g197: BSplineCurve PolesCount=3 KnotsCount=2 Degree=2 IsPeriodic=0
    g198: BSplineCurve PolesCount=2 KnotsCount=2 Degree=1 IsPeriodic=0
    g199: BSplineCurve PolesCount=3 KnotsCount=2 Degree=2 IsPeriodic=0
    g200: BSplineCurve PolesCount=3 KnotsCount=2 Degree=2 IsPeriodic=0
    g201: BSplineCurve PolesCount=3 KnotsCount=2 Degree=2 IsPeriodic=0
    g202: BSplineCurve PolesCount=3 KnotsCount=2 Degree=2 IsPeriodic=0
    g203: BSplineCurve PolesCount=3 KnotsCount=2 Degree=2 IsPeriodic=0
    g204: BSplineCurve PolesCount=3 KnotsCount=2 Degree=2 IsPeriodic=0
    g205: BSplineCurve PolesCount=2 KnotsCount=2 Degree=1 IsPeriodic=0
    g206: BSplineCurve PolesCount=3 KnotsCount=2 Degree=2 IsPeriodic=0
    g207: BSplineCurve PolesCount=3 KnotsCount=2 Degree=2 IsPeriodic=0
    g208: BSplineCurve PolesCount=2 KnotsCount=2 Degree=1 IsPeriodic=0
    g209: BSplineCurve PolesCount=2 KnotsCount=2 Degree=1 IsPeriodic=0
    g210: BSplineCurve PolesCount=2 KnotsCount=2 Degree=1 IsPeriodic=0
    g211: BSplineCurve PolesCount=2 KnotsCount=2 Degree=1 IsPeriodic=0
    g212: BSplineCurve PolesCount=2 KnotsCount=2 Degree=1 IsPeriodic=0
    g213: BSplineCurve PolesCount=2 KnotsCount=2 Degree=1 IsPeriodic=0
    g214: BSplineCurve PolesCount=2 KnotsCount=2 Degree=1 IsPeriodic=0
    g215: BSplineCurve PolesCount=2 KnotsCount=2 Degree=1 IsPeriodic=0
    g216: BSplineCurve PolesCount=2 KnotsCount=2 Degree=1 IsPeriodic=0
    g217: BSplineCurve PolesCount=2 KnotsCount=2 Degree=1 IsPeriodic=0
    g218: BSplineCurve PolesCount=2 KnotsCount=2 Degree=1 IsPeriodic=0
    g219: BSplineCurve PolesCount=2 KnotsCount=2 Degree=1 IsPeriodic=0
    g220: BSplineCurve PolesCount=2 KnotsCount=2 Degree=1 IsPeriodic=0
    g221: BSplineCurve PolesCount=2 KnotsCount=2 Degree=1 IsPeriodic=0
    g222: BSplineCurve PolesCount=2 KnotsCount=2 Degree=1 IsPeriodic=0
    g223: BSplineCurve PolesCount=2 KnotsCount=2 Degree=1 IsPeriodic=0
    g224: BSplineCurve PolesCount=3 KnotsCount=2 Degree=2 IsPeriodic=0
    g225: BSplineCurve PolesCount=3 KnotsCount=2 Degree=2 IsPeriodic=0
    g226: BSplineCurve PolesCount=3 KnotsCount=2 Degree=2 IsPeriodic=0
    g227: BSplineCurve PolesCount=3 KnotsCount=2 Degree=2 IsPeriodic=0
    g228: BSplineCurve PolesCount=3 KnotsCount=2 Degree=2 IsPeriodic=0
    g229: BSplineCurve PolesCount=3 KnotsCount=2 Degree=2 IsPeriodic=0
    g230: BSplineCurve PolesCount=2 KnotsCount=2 Degree=1 IsPeriodic=0
    g231: BSplineCurve PolesCount=3 KnotsCount=2 Degree=2 IsPeriodic=0
    g232: BSplineCurve PolesCount=3 KnotsCount=2 Degree=2 IsPeriodic=0
    g233: BSplineCurve PolesCount=3 KnotsCount=2 Degree=2 IsPeriodic=0
    g234: BSplineCurve PolesCount=3 KnotsCount=2 Degree=2 IsPeriodic=0
    g235: BSplineCurve PolesCount=3 KnotsCount=2 Degree=2 IsPeriodic=0
    g236: BSplineCurve PolesCount=3 KnotsCount=2 Degree=2 IsPeriodic=0
    g237: BSplineCurve PolesCount=3 KnotsCount=2 Degree=2 IsPeriodic=0
    g238: BSplineCurve PolesCount=2 KnotsCount=2 Degree=1 IsPeriodic=0
    g239: BSplineCurve PolesCount=2 KnotsCount=2 Degree=1 IsPeriodic=0
    g240: BSplineCurve PolesCount=2 KnotsCount=2 Degree=1 IsPeriodic=0
    g241: BSplineCurve PolesCount=2 KnotsCount=2 Degree=1 IsPeriodic=0
    g242: BSplineCurve PolesCount=2 KnotsCount=2 Degree=1 IsPeriodic=0
    g243: BSplineCurve PolesCount=2 KnotsCount=2 Degree=1 IsPeriodic=0
    g244: BSplineCurve PolesCount=3 KnotsCount=2 Degree=2 IsPeriodic=0
    g245: BSplineCurve PolesCount=3 KnotsCount=2 Degree=2 IsPeriodic=0
    g246: BSplineCurve PolesCount=3 KnotsCount=2 Degree=2 IsPeriodic=0
    g247: BSplineCurve PolesCount=3 KnotsCount=2 Degree=2 IsPeriodic=0
    g248: BSplineCurve PolesCount=3 KnotsCount=2 Degree=2 IsPeriodic=0
    g249: BSplineCurve PolesCount=3 KnotsCount=2 Degree=2 IsPeriodic=0
    g250: BSplineCurve PolesCount=3 KnotsCount=2 Degree=2 IsPeriodic=0
    g251: BSplineCurve PolesCount=3 KnotsCount=2 Degree=2 IsPeriodic=0
    g252: BSplineCurve PolesCount=3 KnotsCount=2 Degree=2 IsPeriodic=0
    g253: BSplineCurve PolesCount=3 KnotsCount=2 Degree=2 IsPeriodic=0
    g254: BSplineCurve PolesCount=3 KnotsCount=2 Degree=2 IsPeriodic=0
    g255: BSplineCurve PolesCount=3 KnotsCount=2 Degree=2 IsPeriodic=0
    g256: BSplineCurve PolesCount=3 KnotsCount=2 Degree=2 IsPeriodic=0
    g257: BSplineCurve PolesCount=3 KnotsCount=2 Degree=2 IsPeriodic=0
    g258: BSplineCurve PolesCount=3 KnotsCount=2 Degree=2 IsPeriodic=0
    g259: BSplineCurve PolesCount=3 KnotsCount=2 Degree=2 IsPeriodic=0
    g260: BSplineCurve PolesCount=3 KnotsCount=2 Degree=2 IsPeriodic=0
    g261: BSplineCurve PolesCount=2 KnotsCount=2 Degree=1 IsPeriodic=0
    g262: BSplineCurve PolesCount=3 KnotsCount=2 Degree=2 IsPeriodic=0
    g263: BSplineCurve PolesCount=3 KnotsCount=2 Degree=2 IsPeriodic=0
    g264: BSplineCurve PolesCount=3 KnotsCount=2 Degree=2 IsPeriodic=0
    g265: BSplineCurve PolesCount=3 KnotsCount=2 Degree=2 IsPeriodic=0
    g266: BSplineCurve PolesCount=3 KnotsCount=2 Degree=2 IsPeriodic=0
    g267: BSplineCurve PolesCount=3 KnotsCount=2 Degree=2 IsPeriodic=0
    g268: BSplineCurve PolesCount=3 KnotsCount=2 Degree=2 IsPeriodic=0
    g269: BSplineCurve PolesCount=3 KnotsCount=2 Degree=2 IsPeriodic=0
    g270: BSplineCurve PolesCount=3 KnotsCount=2 Degree=2 IsPeriodic=0
    g271: BSplineCurve PolesCount=3 KnotsCount=2 Degree=2 IsPeriodic=0
    g272: BSplineCurve PolesCount=3 KnotsCount=2 Degree=2 IsPeriodic=0
    g273: BSplineCurve PolesCount=2 KnotsCount=2 Degree=1 IsPeriodic=0
    g274: BSplineCurve PolesCount=3 KnotsCount=2 Degree=2 IsPeriodic=0
    g275: BSplineCurve PolesCount=3 KnotsCount=2 Degree=2 IsPeriodic=0
    g276: BSplineCurve PolesCount=2 KnotsCount=2 Degree=1 IsPeriodic=0
    g277: BSplineCurve PolesCount=2 KnotsCount=2 Degree=1 IsPeriodic=0
    g278: BSplineCurve PolesCount=2 KnotsCount=2 Degree=1 IsPeriodic=0
    g279: BSplineCurve PolesCount=2 KnotsCount=2 Degree=1 IsPeriodic=0
    g280: BSplineCurve PolesCount=3 KnotsCount=2 Degree=2 IsPeriodic=0
    g281: BSplineCurve PolesCount=3 KnotsCount=2 Degree=2 IsPeriodic=0
    g282: BSplineCurve PolesCount=3 KnotsCount=2 Degree=2 IsPeriodic=0
    g283: BSplineCurve PolesCount=3 KnotsCount=2 Degree=2 IsPeriodic=0
    g284: BSplineCurve PolesCount=3 KnotsCount=2 Degree=2 IsPeriodic=0
    g285: BSplineCurve PolesCount=2 KnotsCount=2 Degree=1 IsPeriodic=0
    g286: BSplineCurve PolesCount=3 KnotsCount=2 Degree=2 IsPeriodic=0
    g287: BSplineCurve PolesCount=3 KnotsCount=2 Degree=2 IsPeriodic=0
    g288: BSplineCurve PolesCount=3 KnotsCount=2 Degree=2 IsPeriodic=0
    g289: BSplineCurve PolesCount=3 KnotsCount=2 Degree=2 IsPeriodic=0
    g290: BSplineCurve PolesCount=3 KnotsCount=2 Degree=2 IsPeriodic=0
    g291: BSplineCurve PolesCount=3 KnotsCount=2 Degree=2 IsPeriodic=0
    g292: BSplineCurve PolesCount=2 KnotsCount=2 Degree=1 IsPeriodic=0
    g293: BSplineCurve PolesCount=3 KnotsCount=2 Degree=2 IsPeriodic=0
    g294: BSplineCurve PolesCount=3 KnotsCount=2 Degree=2 IsPeriodic=0
    g295: BSplineCurve PolesCount=3 KnotsCount=2 Degree=2 IsPeriodic=0
    g296: BSplineCurve PolesCount=3 KnotsCount=2 Degree=2 IsPeriodic=0
    g297: BSplineCurve PolesCount=3 KnotsCount=2 Degree=2 IsPeriodic=0
    g298: BSplineCurve PolesCount=3 KnotsCount=2 Degree=2 IsPeriodic=0
    g299: BSplineCurve PolesCount=3 KnotsCount=2 Degree=2 IsPeriodic=0
    g300: BSplineCurve PolesCount=3 KnotsCount=2 Degree=2 IsPeriodic=0
    g301: BSplineCurve PolesCount=3 KnotsCount=2 Degree=2 IsPeriodic=0
    g302: BSplineCurve PolesCount=3 KnotsCount=2 Degree=2 IsPeriodic=0
    g303: BSplineCurve PolesCount=3 KnotsCount=2 Degree=2 IsPeriodic=0
    g304: BSplineCurve PolesCount=3 KnotsCount=2 Degree=2 IsPeriodic=0
    g305: BSplineCurve PolesCount=3 KnotsCount=2 Degree=2 IsPeriodic=0
    g306: BSplineCurve PolesCount=3 KnotsCount=2 Degree=2 IsPeriodic=0
    g307: BSplineCurve PolesCount=3 KnotsCount=2 Degree=2 IsPeriodic=0
    g308: BSplineCurve PolesCount=3 KnotsCount=2 Degree=2 IsPeriodic=0
    g309: BSplineCurve PolesCount=3 KnotsCount=2 Degree=2 IsPeriodic=0
    g310: BSplineCurve PolesCount=3 KnotsCount=2 Degree=2 IsPeriodic=0
    g311: BSplineCurve PolesCount=3 KnotsCount=2 Degree=2 IsPeriodic=0
    g312: BSplineCurve PolesCount=3 KnotsCount=2 Degree=2 IsPeriodic=0
    g313: BSplineCurve PolesCount=3 KnotsCount=2 Degree=2 IsPeriodic=0
    g314: BSplineCurve PolesCount=3 KnotsCount=2 Degree=2 IsPeriodic=0
    g315: BSplineCurve PolesCount=3 KnotsCount=2 Degree=2 IsPeriodic=0
    g316: BSplineCurve PolesCount=3 KnotsCount=2 Degree=2 IsPeriodic=0
    g317: BSplineCurve PolesCount=3 KnotsCount=2 Degree=2 IsPeriodic=0
    g318: BSplineCurve PolesCount=3 KnotsCount=2 Degree=2 IsPeriodic=0
    g319: BSplineCurve PolesCount=3 KnotsCount=2 Degree=2 IsPeriodic=0
    g320: BSplineCurve PolesCount=2 KnotsCount=2 Degree=1 IsPeriodic=0
    g321: BSplineCurve PolesCount=3 KnotsCount=2 Degree=2 IsPeriodic=0
    g322: BSplineCurve PolesCount=3 KnotsCount=2 Degree=2 IsPeriodic=0
    g323: BSplineCurve PolesCount=3 KnotsCount=2 Degree=2 IsPeriodic=0
    g324: BSplineCurve PolesCount=3 KnotsCount=2 Degree=2 IsPeriodic=0
    g325: BSplineCurve PolesCount=3 KnotsCount=2 Degree=2 IsPeriodic=0
    g326: BSplineCurve PolesCount=3 KnotsCount=2 Degree=2 IsPeriodic=0
    g327: BSplineCurve PolesCount=3 KnotsCount=2 Degree=2 IsPeriodic=0
    g328: BSplineCurve PolesCount=3 KnotsCount=2 Degree=2 IsPeriodic=0
    g329: BSplineCurve PolesCount=3 KnotsCount=2 Degree=2 IsPeriodic=0
    g330: BSplineCurve PolesCount=3 KnotsCount=2 Degree=2 IsPeriodic=0
    g331: BSplineCurve PolesCount=3 KnotsCount=2 Degree=2 IsPeriodic=0
    g332: BSplineCurve PolesCount=3 KnotsCount=2 Degree=2 IsPeriodic=0
    g333: BSplineCurve PolesCount=3 KnotsCount=2 Degree=2 IsPeriodic=0
    g334: BSplineCurve PolesCount=3 KnotsCount=2 Degree=2 IsPeriodic=0
    g335: BSplineCurve PolesCount=3 KnotsCount=2 Degree=2 IsPeriodic=0
    g336: BSplineCurve PolesCount=3 KnotsCount=2 Degree=2 IsPeriodic=0
    g337: BSplineCurve PolesCount=2 KnotsCount=2 Degree=1 IsPeriodic=0
    g338: BSplineCurve PolesCount=2 KnotsCount=2 Degree=1 IsPeriodic=0
    g339: BSplineCurve PolesCount=2 KnotsCount=2 Degree=1 IsPeriodic=0
    g340: BSplineCurve PolesCount=2 KnotsCount=2 Degree=1 IsPeriodic=0
    g341: BSplineCurve PolesCount=2 KnotsCount=2 Degree=1 IsPeriodic=0
    g342: BSplineCurve PolesCount=2 KnotsCount=2 Degree=1 IsPeriodic=0
    g343: BSplineCurve PolesCount=2 KnotsCount=2 Degree=1 IsPeriodic=0
    g344: BSplineCurve PolesCount=2 KnotsCount=2 Degree=1 IsPeriodic=0
    g345: BSplineCurve PolesCount=2 KnotsCount=2 Degree=1 IsPeriodic=0
    g346: BSplineCurve PolesCount=2 KnotsCount=2 Degree=1 IsPeriodic=0
    g347: BSplineCurve PolesCount=2 KnotsCount=2 Degree=1 IsPeriodic=0
    g348: BSplineCurve PolesCount=3 KnotsCount=2 Degree=2 IsPeriodic=0
    g349: BSplineCurve PolesCount=3 KnotsCount=2 Degree=2 IsPeriodic=0
    g350: BSplineCurve PolesCount=3 KnotsCount=2 Degree=2 IsPeriodic=0
    g351: BSplineCurve PolesCount=3 KnotsCount=2 Degree=2 IsPeriodic=0
    g352: BSplineCurve PolesCount=3 KnotsCount=2 Degree=2 IsPeriodic=0
    g353: BSplineCurve PolesCount=3 KnotsCount=2 Degree=2 IsPeriodic=0
    g354: BSplineCurve PolesCount=3 KnotsCount=2 Degree=2 IsPeriodic=0
    g355: BSplineCurve PolesCount=3 KnotsCount=2 Degree=2 IsPeriodic=0
    g356: BSplineCurve PolesCount=3 KnotsCount=2 Degree=2 IsPeriodic=0
    g357: BSplineCurve PolesCount=3 KnotsCount=2 Degree=2 IsPeriodic=0
    g358: BSplineCurve PolesCount=3 KnotsCount=2 Degree=2 IsPeriodic=0
    g359: BSplineCurve PolesCount=3 KnotsCount=2 Degree=2 IsPeriodic=0
    g360: BSplineCurve PolesCount=3 KnotsCount=2 Degree=2 IsPeriodic=0
    g361: BSplineCurve PolesCount=3 KnotsCount=2 Degree=2 IsPeriodic=0
    g362: BSplineCurve PolesCount=3 KnotsCount=2 Degree=2 IsPeriodic=0
    g363: BSplineCurve PolesCount=3 KnotsCount=2 Degree=2 IsPeriodic=0
    g364: BSplineCurve PolesCount=2 KnotsCount=2 Degree=1 IsPeriodic=0
    g365: BSplineCurve PolesCount=2 KnotsCount=2 Degree=1 IsPeriodic=0
    g366: BSplineCurve PolesCount=2 KnotsCount=2 Degree=1 IsPeriodic=0
    g367: BSplineCurve PolesCount=2 KnotsCount=2 Degree=1 IsPeriodic=0
    g368: BSplineCurve PolesCount=2 KnotsCount=2 Degree=1 IsPeriodic=0
    g369: BSplineCurve PolesCount=2 KnotsCount=2 Degree=1 IsPeriodic=0
    g370: BSplineCurve PolesCount=2 KnotsCount=2 Degree=1 IsPeriodic=0
    g371: BSplineCurve PolesCount=2 KnotsCount=2 Degree=1 IsPeriodic=0
    g372: BSplineCurve PolesCount=2 KnotsCount=2 Degree=1 IsPeriodic=0
    g373: BSplineCurve PolesCount=2 KnotsCount=2 Degree=1 IsPeriodic=0
    g374: BSplineCurve PolesCount=2 KnotsCount=2 Degree=1 IsPeriodic=0
    g375: BSplineCurve PolesCount=2 KnotsCount=2 Degree=1 IsPeriodic=0
    g376: BSplineCurve PolesCount=2 KnotsCount=2 Degree=1 IsPeriodic=0
    g377: BSplineCurve PolesCount=2 KnotsCount=2 Degree=1 IsPeriodic=0
    g378: BSplineCurve PolesCount=2 KnotsCount=2 Degree=1 IsPeriodic=0
    g379: BSplineCurve PolesCount=2 KnotsCount=2 Degree=1 IsPeriodic=0
    g380: BSplineCurve PolesCount=2 KnotsCount=2 Degree=1 IsPeriodic=0
    g381: BSplineCurve PolesCount=2 KnotsCount=2 Degree=1 IsPeriodic=0
    g382: BSplineCurve PolesCount=2 KnotsCount=2 Degree=1 IsPeriodic=0
    g383: BSplineCurve PolesCount=2 KnotsCount=2 Degree=1 IsPeriodic=0
    g384: BSplineCurve PolesCount=2 KnotsCount=2 Degree=1 IsPeriodic=0
    g385: BSplineCurve PolesCount=2 KnotsCount=2 Degree=1 IsPeriodic=0
    g386: BSplineCurve PolesCount=2 KnotsCount=2 Degree=1 IsPeriodic=0
    g387: BSplineCurve PolesCount=2 KnotsCount=2 Degree=1 IsPeriodic=0
    g388: BSplineCurve PolesCount=2 KnotsCount=2 Degree=1 IsPeriodic=0
    g389: BSplineCurve PolesCount=2 KnotsCount=2 Degree=1 IsPeriodic=0
    g390: BSplineCurve PolesCount=2 KnotsCount=2 Degree=1 IsPeriodic=0
    g391: BSplineCurve PolesCount=2 KnotsCount=2 Degree=1 IsPeriodic=0
    g392: BSplineCurve PolesCount=2 KnotsCount=2 Degree=1 IsPeriodic=0
    g393: BSplineCurve PolesCount=2 KnotsCount=2 Degree=1 IsPeriodic=0
    g394: BSplineCurve PolesCount=2 KnotsCount=2 Degree=1 IsPeriodic=0
    g395: BSplineCurve PolesCount=2 KnotsCount=2 Degree=1 IsPeriodic=0
    g396: BSplineCurve PolesCount=2 KnotsCount=2 Degree=1 IsPeriodic=0
    g397: BSplineCurve PolesCount=2 KnotsCount=2 Degree=1 IsPeriodic=0
    g398: BSplineCurve PolesCount=3 KnotsCount=2 Degree=2 IsPeriodic=0
    g399: BSplineCurve PolesCount=3 KnotsCount=2 Degree=2 IsPeriodic=0
    ... +790 more geometry lines
  constraints (1190):
    c: Coincident(g93,g94)
    c: Coincident(g92,g93)
    c: Coincident(g282,g284)
    c: Coincident(g273,g274)
    c: Coincident(g272,g273)
    c: Coincident(g280,g282)
    c: Coincident(g88,g89)
    c: Coincident(g96,g97)
    c: Coincident(g299,g300)
    c: Coincident(g284,g286)
    c: Coincident(g298,g299)
    c: Coincident(g96,g99)
    c: Coincident(g89,g90)
    c: Coincident(g280,g281)
    c: Coincident(g271,g272)
    c: Coincident(g298,g304)
    c: Coincident(g300,g301)
    c: Coincident(g286,g288)
    c: Coincident(g274,g275)
    c: Coincident(g281,g283)
    c: Coincident(g303,g304)
    c: Coincident(g301,g302)
    c: Coincident(g288,g290)
    c: Coincident(g302,g303)
    c: Coincident(g283,g285)
    c: Coincident(g285,g287)
    c: Coincident(g290,g292)
    c: Coincident(g292,g294)
    c: Coincident(g270,g271)
    c: Coincident(g306,g308)
    c: Coincident(g287,g289)
    c: Coincident(g249,g251)
    c: Coincident(g314,g316)
    c: Coincident(g305,g306)
    c: Coincident(g308,g310)
    c: Coincident(g294,g296)
    c: Coincident(g251,g253)
    c: Coincident(g312,g314)
    c: Coincident(g263,g264)
    c: Coincident(g322,g324)
    c: Coincident(g316,g318)
    c: Coincident(g264,g265)
    c: Coincident(g289,g291)
    c: Coincident(g305,g307)
    c: Coincident(g324,g326)
    c: Coincident(g247,g249)
    c: Coincident(g310,g311)
    c: Coincident(g296,g297)
    c: Coincident(g262,g263)
    c: Coincident(g276,g277)
    c: Coincident(g320,g322)
    c: Coincident(g318,g320)
    c: Coincident(g265,g266)
    c: Coincident(g309,g311)
    c: Coincident(g275,g276)
    c: Coincident(g307,g309)
    c: Coincident(g291,g293)
    c: Coincident(g270,g279)
    c: Coincident(g325,g327)
    c: Coincident(g323,g325)
    c: Coincident(g100,g101)
    c: Coincident(g84,g85)
    c: Coincident(g253,g255)
    c: Coincident(g295,g297)
    c: Coincident(g277,g278)
    c: Coincident(g262,g269)
    c: Coincident(g312,g313)
    c: Coincident(g326,g327)
    c: Coincident(g247,g248)
    c: Coincident(g293,g295)
    c: Coincident(g329,g330)
    c: Coincident(g330,g331)
    c: Coincident(g278,g279)
    c: Coincident(g254,g256)
    c: Coincident(g266,g267)
    c: Coincident(g85,g86)
    c: Coincident(g100,g103)
    c: Coincident(g328,g329)
    c: Coincident(g321,g323)
    c: Coincident(g268,g269)
    c: Coincident(g267,g268)
    c: Coincident(g331,g332)
    c: Coincident(g94,g95)
    c: Coincident(g92,g95)
    c: Coincident(g252,g254)
    c: Coincident(g328,g336)
    c: Coincident(g248,g250)
    c: Coincident(g250,g252)
    c: Coincident(g332,g333)
    c: Coincident(g256,g258)
    c: Coincident(g319,g321)
    c: Coincident(g335,g336)
    c: Coincident(g255,g257)
    c: Coincident(g313,g315)
    c: Coincident(g88,g91)
    c: Coincident(g97,g98)
    c: Coincident(g260,g261)
    c: Coincident(g98,g99)
    c: Coincident(g90,g91)
    c: Coincident(g333,g334)
    c: Coincident(g259,g261)
    c: Coincident(g334,g335)
    c: Coincident(g258,g260)
    c: Coincident(g317,g319)
    c: Coincident(g348,g350)
    c: Coincident(g350,g352)
    c: Coincident(g315,g317)
    c: Coincident(g257,g259)
    c: Coincident(g357,g358)
    c: Coincident(g356,g357)
    c: Coincident(g228,g229)
    c: Coincident(g227,g228)
    c: Coincident(g346,g347)
    c: Coincident(g229,g230)
    c: Coincident(g352,g354)
    c: Coincident(g358,g359)
    c: Coincident(g231,g232)
    c: Coincident(g348,g349)
    c: Coincident(g230,g231)
    c: Coincident(g345,g346)
    c: Coincident(g356,g363)
    c: Coincident(g226,g227)
    c: Coincident(g232,g233)
    c: Coincident(g344,g345)
    c: Coincident(g238,g239)
    c: Coincident(g338,g339)
    c: Coincident(g237,g238)
    c: Coincident(g337,g347)
    c: Coincident(g359,g360)
    c: Coincident(g233,g234)
    c: Coincident(g236,g237)
    c: Coincident(g101,g102)
    c: Coincident(g84,g87)
    c: Coincident(g354,g355)
    c: Coincident(g243,g244)
    c: Coincident(g337,g338)
    c: Coincident(g362,g363)
    c: Coincident(g226,g246)
    c: Coincident(g349,g351)
    c: Coincident(g235,g236)
    c: Coincident(g234,g235)
    c: Coincident(g102,g103)
    c: Coincident(g86,g87)
    c: Coincident(g244,g245)
    c: Coincident(g80,g81)
    c: Coincident(g104,g105)
    c: Coincident(g245,g246)
    c: Coincident(g360,g361)
    c: Coincident(g361,g362)
    c: Coincident(g351,g353)
    c: Coincident(g242,g243)
    c: Coincident(g353,g355)
    c: Coincident(g239,g240)
    c: Coincident(g81,g82)
    c: Coincident(g104,g107)
    c: Coincident(g241,g242)
    c: Coincident(g340,g341)
    c: Coincident(g339,g340)
    c: Coincident(g240,g241)
    c: Coincident(g343,g344)
    c: Coincident(g341,g342)
    c: Coincident(g342,g343)
    c: Coincident(g384,g385)
    c: Coincident(g383,g384)
    c: Coincident(g382,g383)
    c: Coincident(g376,g377)
    c: Coincident(g214,g216)
    c: Coincident(g375,g385)
    c: Coincident(g373,g374)
    c: Coincident(g216,g218)
    c: Coincident(g80,g83)
    c: Coincident(g105,g106)
    c: Coincident(g375,g376)
    c: Coincident(g210,g212)
    c: Coincident(g220,g221)
    c: Coincident(g372,g373)
    c: Coincident(g221,g222)
    c: Coincident(g208,g210)
    c: Coincident(g222,g223)
    c: Coincident(g106,g107)
    c: Coincident(g82,g83)
    c: Coincident(g212,g214)
    c: Coincident(g371,g372)
    c: Coincident(g208,g209)
    c: Coincident(g219,g220)
    c: Coincident(g365,g366)
    c: Coincident(g213,g215)
    c: Coincident(g209,g211)
    c: Coincident(g364,g374)
    c: Coincident(g377,g378)
    c: Coincident(g211,g213)
    c: Coincident(g364,g365)
    c: Coincident(g381,g382)
    c: Coincident(g378,g379)
    c: Coincident(g380,g381)
    c: Coincident(g379,g380)
    c: Coincident(g223,g224)
    c: Coincident(g224,g225)
    c: Coincident(g219,g225)
    c: Coincident(g217,g218)
    c: Coincident(g108,g109)
    c: Coincident(g76,g77)
    c: Coincident(g215,g217)
    c: Coincident(g366,g367)
    c: Coincident(g370,g371)
    c: Coincident(g367,g368)
    c: Coincident(g369,g370)
    c: Coincident(g368,g369)
    c: Coincident(g108,g111)
    c: Coincident(g77,g78)
    c: Coincident(g419,g420)
    c: Coincident(g418,g419)
    c: Coincident(g109,g110)
    c: Coincident(g76,g79)
    c: Coincident(g78,g79)
    c: Coincident(g110,g111)
    c: Coincident(g181,g182)
    c: Coincident(g414,g415)
    c: Coincident(g413,g414)
    c: Coincident(g415,g416)
    c: Coincident(g182,g183)
    c: Coincident(g417,g418)
    c: Coincident(g412,g413)
    c: Coincident(g416,g417)
    c: Coincident(g397,g420)
    c: Coincident(g401,g402)
    c: Coincident(g402,g403)
    c: Coincident(g400,g401)
    c: Coincident(g180,g181)
    c: Coincident(g397,g398)
    c: Coincident(g183,g184)
    c: Coincident(g403,g404)
    c: Coincident(g399,g400)
    c: Coincident(g398,g399)
    c: Coincident(g395,g396)
    c: Coincident(g184,g185)
    c: Coincident(g411,g412)
    c: Coincident(g394,g395)
    c: Coincident(g404,g405)
    c: Coincident(g189,g190)
    c: Coincident(g185,g186)
    c: Coincident(g198,g199)
    c: Coincident(g179,g180)
    c: Coincident(g188,g189)
    c: Coincident(g405,g406)
    c: Coincident(g190,g191)
    c: Coincident(g407,g408)
    c: Coincident(g393,g394)
    c: Coincident(g197,g198)
    c: Coincident(g191,g192)
    c: Coincident(g410,g411)
    c: Coincident(g406,g407)
    c: Coincident(g186,g187)
    c: Coincident(g187,g188)
    c: Coincident(g205,g206)
    c: Coincident(g204,g205)
    c: Coincident(g387,g388)
    c: Coincident(g408,g409)
    c: Coincident(g199,g200)
    c: Coincident(g179,g207)
    c: Coincident(g196,g197)
    c: Coincident(g409,g410)
    c: Coincident(g192,g193)
    c: Coincident(g206,g207)
    c: Coincident(g386,g396)
    c: Coincident(g195,g196)
    c: Coincident(g203,g204)
    c: Coincident(g386,g387)
    c: Coincident(g193,g194)
    c: Coincident(g200,g201)
    c: Coincident(g194,g195)
    c: Coincident(g202,g203)
    c: Coincident(g201,g202)
    c: Coincident(g392,g393)
    c: Coincident(g388,g389)
    c: Coincident(g391,g392)
    c: Coincident(g389,g390)
    c: Coincident(g112,g113)
    c: Coincident(g72,g73)
    c: Coincident(g390,g391)
    c: Coincident(g73,g74)
    c: Coincident(g112,g115)
    c: Coincident(g72,g75)
    c: Coincident(g113,g114)
    c: Coincident(g432,g433)
    c: Coincident(g432,g460)
    c: Coincident(g74,g75)
    c: Coincident(g114,g115)
    c: Coincident(g438,g439)
    c: Coincident(g439,g440)
    c: Coincident(g459,g460)
    c: Coincident(g433,g434)
    c: Coincident(g437,g438)
    c: Coincident(g456,g457)
    c: Coincident(g440,g441)
    c: Coincident(g155,g178)
    c: Coincident(g455,g456)
    c: Coincident(g155,g156)
    c: Coincident(g458,g459)
    c: Coincident(g457,g458)
    c: Coincident(g445,g446)
    c: Coincident(g446,g447)
    c: Coincident(g434,g435)
    c: Coincident(g175,g176)
    c: Coincident(g454,g455)
    c: Coincident(g441,g442)
    c: Coincident(g156,g157)
    c: Coincident(g447,g448)
    c: Coincident(g444,g445)
    c: Coincident(g442,g443)
    c: Coincident(g436,g437)
    c: Coincident(g174,g175)
    c: Coincident(g443,g444)
    c: Coincident(g157,g158)
    c: Coincident(g430,g431)
    c: Coincident(g166,g167)
    c: Coincident(g435,g436)
    c: Coincident(g448,g449)
    c: Coincident(g429,g430)
    c: Coincident(g453,g454)
    c: Coincident(g173,g174)
    c: Coincident(g450,g451)
    c: Coincident(g449,g450)
    c: Coincident(g165,g166)
    c: Coincident(g158,g159)
    c: Coincident(g167,g168)
    c: Coincident(g164,g165)
    c: Coincident(g451,g452)
    c: Coincident(g452,g453)
    c: Coincident(g177,g178)
    c: Coincident(g159,g160)
    c: Coincident(g428,g429)
    c: Coincident(g176,g177)
    c: Coincident(g172,g173)
    c: Coincident(g163,g164)
    c: Coincident(g160,g161)
    c: Coincident(g422,g423)
    c: Coincident(g168,g169)
    c: Coincident(g161,g162)
    c: Coincident(g162,g163)
    c: Coincident(g171,g172)
    c: Coincident(g421,g431)
    c: Coincident(g170,g171)
    c: Coincident(g169,g170)
    c: Coincident(g421,g422)
    c: Coincident(g427,g428)
    c: Coincident(g423,g424)
    c: Coincident(g426,g427)
    c: Coincident(g424,g425)
    c: Coincident(g425,g426)
    c: Coincident(g68,g69)
    c: Coincident(g116,g117)
    c: Coincident(g116,g119)
    c: Coincident(g69,g70)
    c: Coincident(g68,g71)
    c: Coincident(g117,g118)
    c: Coincident(g118,g119)
    c: Coincident(g70,g71)
    c: Coincident(g473,g475)
    c: Coincident(g475,g477)
    c: Coincident(g472,g474)
    c: Coincident(g472,g473)
    c: Coincident(g477,g479)
    c: Coincident(g474,g476)
    c: Coincident(g476,g478)
    c: Coincident(g483,g484)
    c: Coincident(g479,g481)
    c: Coincident(g144,g154)
    c: Coincident(g144,g145)
    c: Coincident(g483,g489)
    c: Coincident(g488,g489)
    c: Coincident(g487,g488)
    c: Coincident(g481,g482)
    c: Coincident(g486,g487)
    c: Coincident(g485,g486)
    c: Coincident(g484,g485)
    c: Coincident(g147,g148)
    c: Coincident(g148,g149)
    c: Coincident(g145,g146)
    c: Coincident(g478,g480)
    c: Coincident(g480,g482)
    c: Coincident(g470,g471)
    c: Coincident(g469,g470)
    c: Coincident(g151,g152)
    c: Coincident(g146,g147)
    c: Coincident(g149,g150)
    c: Coincident(g153,g154)
    c: Coincident(g468,g469)
    c: Coincident(g152,g153)
    c: Coincident(g150,g151)
    c: Coincident(g462,g463)
    c: Coincident(g467,g468)
    c: Coincident(g461,g471)
    c: Coincident(g463,g464)
    c: Coincident(g461,g462)
    c: Coincident(g466,g467)
    c: Coincident(g464,g465)
    c: Coincident(g465,g466)
    c: Coincident(g64,g65)
    c: Coincident(g120,g121)
    c: Coincident(g121,g122)
    c: Coincident(g64,g67)
    c: Coincident(g120,g123)
    c: Coincident(g65,g66)
    c: Coincident(g122,g123)
    c: Coincident(g66,g67)
    c: Coincident(g501,g521)
    c: Coincident(g501,g502)
    c: Coincident(g520,g521)
    c: Coincident(g516,g517)
    c: Coincident(g515,g516)
    c: Coincident(g508,g509)
    c: Coincident(g507,g508)
    c: Coincident(g509,g510)
    c: Coincident(g502,g503)
    c: Coincident(g506,g507)
    c: Coincident(g519,g520)
    c: Coincident(g510,g511)
    c: Coincident(g134,g135)
    c: Coincident(g511,g512)
    c: Coincident(g132,g134)
    c: Coincident(g133,g135)
    c: Coincident(g139,g140)
    c: Coincident(g512,g513)
    c: Coincident(g505,g506)
    c: Coincident(g503,g504)
    c: Coincident(g518,g519)
    c: Coincident(g517,g518)
    c: Coincident(g138,g139)
    c: Coincident(g140,g141)
    c: Coincident(g513,g514)
    c: Coincident(g504,g505)
    c: Coincident(g514,g515)
    c: Coincident(g130,g132)
    c: Coincident(g137,g138)
    c: Coincident(g499,g500)
    c: Coincident(g498,g499)
    c: Coincident(g141,g142)
    c: Coincident(g131,g133)
    c: Coincident(g136,g137)
    c: Coincident(g142,g143)
    c: Coincident(g136,g143)
    c: Coincident(g128,g130)
    c: Coincident(g497,g498)
    c: Coincident(g129,g131)
    c: Coincident(g128,g129)
    c: Coincident(g496,g497)
    c: Coincident(g491,g492)
    c: Coincident(g492,g493)
    c: Coincident(g495,g496)
    c: Coincident(g490,g500)
    c: Coincident(g490,g491)
    c: Coincident(g493,g494)
    c: Coincident(g494,g495)
    c: Coincident(g124,g125)
    c: Coincident(g125,g126)
    c: Coincident(g60,g61)
    c: Coincident(g61,g62)
    c: Coincident(g60,g63)
    c: Coincident(g62,g63)
    c: Coincident(g124,g127)
    c: Coincident(g126,g127)
    c: Coincident(g1169,g1170)
    c: Coincident(g545,g547)
    c: Coincident(g1153,g1154)
    c: Coincident(g533,g534)
    c: Coincident(g1170,g1171)
    c: Coincident(g534,g536)
    c: Coincident(g1168,g1169)
    c: Coincident(g546,g547)
    c: Coincident(g533,g535)
    c: Coincident(g1152,g1153)
    c: Coincident(g548,g555)
    c: Coincident(g1154,g1155)
    c: Coincident(g1167,g1168)
    c: Coincident(g554,g555)
    c: Coincident(g548,g549)
    c: Coincident(g1161,g1162)
    c: Coincident(g1160,g1161)
    c: Coincident(g543,g545)
    c: Coincident(g544,g546)
    c: Coincident(g1171,g1172)
    c: Coincident(g536,g538)
    c: Coincident(g1166,g1167)
    c: Coincident(g1162,g1163)
    c: Coincident(g1159,g1160)
    c: Coincident(g553,g554)
    c: Coincident(g549,g550)
    c: Coincident(g535,g537)
    c: Coincident(g1155,g1156)
    c: Coincident(g1151,g1152)
    c: Coincident(g538,g540)
    c: Coincident(g1165,g1166)
    c: Coincident(g1175,g1176)
    c: Coincident(g1176,g1177)
    c: Coincident(g542,g544)
    c: Coincident(g1163,g1164)
    c: Coincident(g552,g553)
    c: Coincident(g1158,g1159)
    c: Coincident(g1164,g1165)
    c: Coincident(g550,g551)
    c: Coincident(g1172,g1173)
    c: Coincident(g1156,g1157)
    c: Coincident(g541,g543)
    c: Coincident(g540,g542)
    c: Coincident(g551,g552)
    c: Coincident(g1157,g1158)
    c: Coincident(g1174,g1175)
    c: Coincident(g537,g539)
    c: Coincident(g1177,g1178)
    c: Coincident(g1173,g1174)
    c: Coincident(g1150,g1151)
    c: Coincident(g539,g541)
    c: Coincident(g1150,g1178)
    c: Coincident(g1183,g1184)
    c: Coincident(g530,g531)
    c: Coincident(g1182,g1183)
    c: Coincident(g531,g532)
    c: Coincident(g1179,g1180)
    c: Coincident(g1179,g1189)
    c: Coincident(g528,g529)
    c: Coincident(g1184,g1185)
    c: Coincident(g1181,g1182)
    c: Coincident(g529,g530)
    c: Coincident(g527,g528)
    c: Coincident(g1180,g1181)
    c: Coincident(g524,g525)
    c: Coincident(g1185,g1186)
    c: Coincident(g523,g524)
    c: Coincident(g1186,g1187)
    c: Coincident(g526,g527)
    c: Coincident(g525,g526)
    c: Coincident(g522,g523)
    c: Coincident(g522,g532)
    c: Coincident(g1187,g1188)
    c: Coincident(g1188,g1189)
    c: Coincident(g56,g57)
    c: Coincident(g0,g1)
    c: Coincident(g0,g3)
    c: Coincident(g57,g58)
    c: Coincident(g1,g2)
    c: Coincident(g56,g59)
    c: Coincident(g2,g3)
    c: Coincident(g58,g59)
    c: Coincident(g575,g576)
    c: Coincident(g567,g576)
    c: Coincident(g1124,g1125)
    c: Coincident(g1125,g1126)
    c: Coincident(g572,g573)
    c: Coincident(g1123,g1124)
    c: Coincident(g1108,g1109)
    c: Coincident(g1122,g1123)
    c: Coincident(g1126,g1127)
    c: Coincident(g1109,g1110)
    c: Coincident(g1121,g1122)
    c: Coincident(g1116,g1117)
    c: Coincident(g567,g568)
    c: Coincident(g1107,g1108)
    c: Coincident(g1115,g1116)
    c: Coincident(g1117,g1118)
    c: Coincident(g1114,g1115)
    c: Coincident(g1120,g1121)
    c: Coincident(g568,g569)
    c: Coincident(g1118,g1119)
    c: Coincident(g571,g572)
    c: Coincident(g1127,g1128)
    c: Coincident(g1130,g1131)
    c: Coincident(g1131,g1132)
    c: Coincident(g1119,g1120)
    c: Coincident(g1110,g1111)
    c: Coincident(g1106,g1107)
    c: Coincident(g569,g570)
    c: Coincident(g1113,g1114)
    c: Coincident(g574,g575)
    c: Coincident(g573,g574)
    c: Coincident(g1129,g1130)
    c: Coincident(g1128,g1129)
    c: Coincident(g1111,g1112)
    c: Coincident(g1112,g1113)
    c: Coincident(g570,g571)
    c: Coincident(g1132,g1133)
    c: Coincident(g1105,g1106)
    c: Coincident(g1105,g1133)
    c: Coincident(g1139,g1141)
    c: Coincident(g1140,g1141)
    c: Coincident(g1146,g1147)
    c: Coincident(g562,g563)
    c: Coincident(g1145,g1146)
    c: Coincident(g564,g565)
    c: Coincident(g565,g566)
    c: Coincident(g1137,g1139)
    c: Coincident(g1138,g1140)
    c: Coincident(g561,g562)
    c: Coincident(g1147,g1148)
    c: Coincident(g558,g559)
    c: Coincident(g1144,g1145)
    c: Coincident(g563,g564)
    c: Coincident(g1148,g1149)
    c: Coincident(g1143,g1144)
    c: Coincident(g1135,g1137)
    c: Coincident(g1136,g1138)
    c: Coincident(g557,g558)
    c: Coincident(g560,g561)
    c: Coincident(g559,g560)
    c: Coincident(g1142,g1149)
    c: Coincident(g1142,g1143)
    c: Coincident(g1134,g1135)
    c: Coincident(g1134,g1136)
    c: Coincident(g556,g557)
    c: Coincident(g556,g566)
    c: Coincident(g4,g5)
    c: Coincident(g52,g53)
    c: Coincident(g5,g6)
    c: Coincident(g52,g55)
    c: Coincident(g53,g54)
    c: Coincident(g4,g7)
    c: Coincident(g54,g55)
    c: Coincident(g6,g7)
    c: Coincident(g599,g601)
    c: Coincident(g1068,g1069)
    c: Coincident(g1067,g1068)
    c: Coincident(g597,g599)
    c: Coincident(g1065,g1066)
    c: Coincident(g595,g597)
    c: Coincident(g1066,g1067)
    c: Coincident(g613,g615)
    c: Coincident(g601,g603)
    c: Coincident(g1069,g1070)
    c: Coincident(g589,g591)
    c: Coincident(g588,g589)
    c: Coincident(g615,g617)
    c: Coincident(g1064,g1065)
    c: Coincident(g613,g614)
    c: Coincident(g593,g595)
    c: Coincident(g591,g593)
    c: Coincident(g611,g612)
    c: Coincident(g1056,g1057)
    c: Coincident(g1057,g1058)
    c: Coincident(g606,g612)
    c: Coincident(g1056,g1079)
    c: Coincident(g617,g619)
    c: Coincident(g1063,g1064)
    c: Coincident(g1058,g1059)
    c: Coincident(g614,g616)
    c: Coincident(g588,g590)
    c: Coincident(g603,g605)
    c: Coincident(g1070,g1071)
    c: Coincident(g1059,g1060)
    c: Coincident(g610,g611)
    c: Coincident(g1076,g1077)
    c: Coincident(g1075,g1076)
    c: Coincident(g606,g607)
    c: Coincident(g618,g619)
    c: Coincident(g1062,g1063)
    c: Coincident(g1060,g1061)
    c: Coincident(g616,g618)
    c: Coincident(g1061,g1062)
    c: Coincident(g1074,g1075)
    c: Coincident(g600,g602)
    c: Coincident(g598,g600)
    c: Coincident(g604,g605)
    c: Coincident(g1071,g1072)
    c: Coincident(g609,g610)
    c: Coincident(g1073,g1074)
    c: Coincident(g602,g604)
    c: Coincident(g607,g608)
    c: Coincident(g1072,g1073)
    c: Coincident(g590,g592)
    c: Coincident(g596,g598)
    c: Coincident(g608,g609)
    c: Coincident(g1085,g1087)
    c: Coincident(g1087,g1089)
    c: Coincident(g583,g584)
    c: Coincident(g594,g596)
    c: Coincident(g1101,g1102)
    c: Coincident(g592,g594)
    c: Coincident(g1100,g1101)
    c: Coincident(g1083,g1085)
    c: Coincident(g1077,g1078)
    c: Coincident(g582,g583)
    c: Coincident(g1102,g1103)
    c: Coincident(g1089,g1091)
    c: Coincident(g1078,g1079)
    c: Coincident(g579,g580)
    c: Coincident(g1099,g1100)
    c: Coincident(g1086,g1088)
    c: Coincident(g585,g586)
    c: Coincident(g586,g587)
    c: Coincident(g1088,g1090)
    c: Coincident(g1103,g1104)
    c: Coincident(g1098,g1099)
    c: Coincident(g1084,g1086)
    c: Coincident(g1081,g1083)
    c: Coincident(g1091,g1093)
    c: Coincident(g581,g582)
    c: Coincident(g1097,g1098)
    c: Coincident(g584,g585)
    c: Coincident(g1096,g1104)
    c: Coincident(g580,g581)
    c: Coincident(g1096,g1097)
    c: Coincident(g1093,g1095)
    c: Coincident(g1090,g1092)
    c: Coincident(g1094,g1095)
    c: Coincident(g578,g579)
    c: Coincident(g1082,g1084)
    c: Coincident(g1092,g1094)
    c: Coincident(g1080,g1081)
    c: Coincident(g48,g49)
    c: Coincident(g8,g9)
    c: Coincident(g1080,g1082)
    c: Coincident(g577,g578)
    c: Coincident(g577,g587)
    c: Coincident(g9,g10)
    c: Coincident(g48,g51)
    c: Coincident(g8,g11)
    c: Coincident(g49,g50)
    c: Coincident(g1012,g1013)
    c: Coincident(g632,g634)
    c: Coincident(g50,g51)
    c: Coincident(g10,g11)
    c: Coincident(g1011,g1012)
    c: Coincident(g1009,g1010)
    c: Coincident(g1013,g1014)
    c: Coincident(g634,g636)
    c: Coincident(g654,g655)
    c: Coincident(g1010,g1011)
    c: Coincident(g631,g632)
    c: Coincident(g1008,g1009)
    c: Coincident(g653,g654)
    c: Coincident(g647,g655)
    c: Coincident(g647,g648)
    c: Coincident(g645,g646)
    c: Coincident(g1007,g1008)
    c: Coincident(g652,g653)
    c: Coincident(g1014,g1015)
    c: Coincident(g636,g638)
    c: Coincident(g648,g649)
    c: Coincident(g1001,g1002)
    c: Coincident(g644,g646)
    c: Coincident(g1002,g1003)
    c: Coincident(g1006,g1007)
    c: Coincident(g1000,g1001)
    c: Coincident(g1003,g1004)
    c: Coincident(g1005,g1006)
    c: Coincident(g1004,g1005)
    c: Coincident(g649,g650)
    c: Coincident(g651,g652)
    c: Coincident(g631,g633)
    c: Coincident(g1000,g1023)
    c: Coincident(g643,g645)
    c: Coincident(g1019,g1020)
    c: Coincident(g1015,g1016)
    c: Coincident(g1020,g1021)
    c: Coincident(g1018,g1019)
    c: Coincident(g650,g651)
    c: Coincident(g642,g644)
    c: Coincident(g1016,g1017)
    c: Coincident(g638,g640)
    c: Coincident(g1017,g1018)
    c: Coincident(g1039,g1041)
    c: Coincident(g1040,g1041)
    c: Coincident(g626,g627)
    c: Coincident(g640,g642)
    c: Coincident(g1053,g1055)
    c: Coincident(g641,g643)
    c: Coincident(g1037,g1039)
    c: Coincident(g1054,g1055)
    c: Coincident(g625,g626)
    c: Coincident(g639,g641)
    c: Coincident(g633,g635)
    c: Coincident(g1038,g1040)
    c: Coincident(g1051,g1053)
    c: Coincident(g622,g623)
    c: Coincident(g637,g639)
    c: Coincident(g1032,g1034)
    c: Coincident(g1052,g1054)
    c: Coincident(g635,g637)
    c: Coincident(g1036,g1038)
    c: Coincident(g1034,g1036)
    c: Coincident(g1030,g1032)
    c: Coincident(g1021,g1022)
    c: Coincident(g1035,g1037)
    c: Coincident(g1045,g1046)
    c: Coincident(g1022,g1023)
    c: Coincident(g1050,g1052)
    c: Coincident(g1044,g1045)
    c: Coincident(g1049,g1051)
    c: Coincident(g624,g625)
    c: Coincident(g628,g629)
    c: Coincident(g1046,g1047)
    c: Coincident(g1049,g1050)
    c: Coincident(g629,g630)
    c: Coincident(g623,g624)
    c: Coincident(g1033,g1035)
    c: Coincident(g1028,g1030)
    c: Coincident(g1029,g1031)
    c: Coincident(g1027,g1029)
    c: Coincident(g1031,g1033)
    c: Coincident(g1047,g1048)
    c: Coincident(g12,g13)
    c: Coincident(g44,g45)
    c: Coincident(g627,g628)
    c: Coincident(g1025,g1027)
    c: Coincident(g1043,g1044)
    c: Coincident(g621,g622)
    c: Coincident(g1042,g1048)
    c: Coincident(g1026,g1028)
    c: Coincident(g1042,g1043)
    c: Coincident(g44,g47)
    c: Coincident(g13,g14)
    c: Coincident(g1024,g1025)
    c: Coincident(g1024,g1026)
    c: Coincident(g620,g621)
    c: Coincident(g620,g630)
    c: Coincident(g978,g979)
    c: Coincident(g681,g683)
    c: Coincident(g45,g46)
    c: Coincident(g12,g15)
    c: Coincident(g977,g978)
    c: Coincident(g683,g685)
    c: Coincident(g979,g980)
    c: Coincident(g975,g976)
    c: Coincident(g694,g695)
    c: Coincident(g693,g694)
    c: Coincident(g974,g975)
    c: Coincident(g976,g977)
    c: Coincident(g680,g681)
    c: Coincident(g14,g15)
    c: Coincident(g46,g47)
    c: Coincident(g973,g974)
    c: Coincident(g980,g981)
    c: Coincident(g688,g695)
    c: Coincident(g692,g693)
    c: Coincident(g685,g687)
    c: Coincident(g997,g998)
    c: Coincident(g972,g973)
    c: Coincident(g971,g972)
    c: Coincident(g996,g997)
    c: Coincident(g981,g982)
    c: Coincident(g670,g671)
    c: Coincident(g970,g971)
    c: Coincident(g969,g970)
    c: Coincident(g968,g969)
    c: Coincident(g967,g968)
    c: Coincident(g982,g983)
    c: Coincident(g966,g967)
    c: Coincident(g669,g670)
    c: Coincident(g983,g984)
    c: Coincident(g671,g672)
    c: Coincident(g680,g682)
    c: Coincident(g688,g689)
    c: Coincident(g984,g985)
    c: Coincident(g691,g692)
    c: Coincident(g663,g664)
    c: Coincident(g985,g986)
    c: Coincident(g966,g989)
    c: Coincident(g986,g987)
    c: Coincident(g664,g665)
    c: Coincident(g662,g663)
    c: Coincident(g686,g687)
    c: Coincident(g672,g673)
    c: Coincident(g668,g669)
    c: Coincident(g665,g666)
    c: Coincident(g661,g662)
    c: Coincident(g689,g690)
    c: Coincident(g998,g999)
    c: Coincident(g995,g996)
    c: Coincident(g690,g691)
    c: Coincident(g673,g674)
    c: Coincident(g682,g684)
    c: Coincident(g990,g999)
    c: Coincident(g660,g661)
    c: Coincident(g40,g41)
    c: Coincident(g16,g17)
    c: Coincident(g666,g667)
    c: Coincident(g684,g686)
    c: Coincident(g987,g988)
    c: Coincident(g667,g668)
    c: Coincident(g994,g995)
    c: Coincident(g990,g991)
    c: Coincident(g659,g660)
    c: Coincident(g988,g989)
    c: Coincident(g677,g678)
    c: Coincident(g17,g18)
    c: Coincident(g40,g43)
    c: Coincident(g674,g675)
    c: Coincident(g678,g679)
    c: Coincident(g991,g992)
    c: Coincident(g658,g659)
    c: Coincident(g993,g994)
    c: Coincident(g675,g676)
    c: Coincident(g657,g658)
    c: Coincident(g992,g993)
    c: Coincident(g676,g677)
    c: Coincident(g656,g657)
    c: Coincident(g656,g679)
    c: Coincident(g931,g932)
    c: Coincident(g726,g727)
    c: Coincident(g932,g933)
    c: Coincident(g725,g726)
    c: Coincident(g928,g929)
    c: Coincident(g930,g931)
    c: Coincident(g927,g928)
    c: Coincident(g722,g723)
    c: Coincident(g929,g930)
    c: Coincident(g933,g934)
    c: Coincident(g926,g927)
    c: Coincident(g724,g725)
    c: Coincident(g41,g42)
    c: Coincident(g16,g19)
    c: Coincident(g925,g926)
    c: Coincident(g710,g711)
    c: Coincident(g709,g710)
    c: Coincident(g723,g724)
    c: Coincident(g934,g935)
    c: Coincident(g951,g953)
    c: Coincident(g953,g955)
    c: Coincident(g924,g925)
    c: Coincident(g703,g704)
    c: Coincident(g923,g924)
    c: Coincident(g42,g43)
    c: Coincident(g18,g19)
    c: Coincident(g704,g705)
    c: Coincident(g711,g712)
    c: Coincident(g935,g936)
    c: Coincident(g954,g956)
    c: Coincident(g922,g923)
    c: Coincident(g952,g954)
    c: Coincident(g921,g922)
    c: Coincident(g702,g703)
    c: Coincident(g936,g937)
    c: Coincident(g36,g37)
    c: Coincident(g20,g21)
    c: Coincident(g708,g709)
    c: Coincident(g920,g921)
    c: Coincident(g705,g706)
    c: Coincident(g712,g713)
    c: Coincident(g937,g938)
    c: Coincident(g728,g729)
    c: Coincident(g701,g702)
    c: Coincident(g938,g939)
    c: Coincident(g36,g39)
    c: Coincident(g21,g22)
    c: Coincident(g919,g920)
    c: Coincident(g956,g957)
    c: Coincident(g948,g950)
    c: Coincident(g949,g951)
    c: Coincident(g955,g957)
    c: Coincident(g939,g940)
    c: Coincident(g706,g707)
    c: Coincident(g946,g948)
    c: Coincident(g950,g952)
    c: Coincident(g713,g714)
    c: Coincident(g729,g730)
    c: Coincident(g919,g942)
    c: Coincident(g727,g728)
    c: Coincident(g700,g701)
    c: Coincident(g707,g708)
    c: Coincident(g962,g963)
    c: Coincident(g963,g964)
    c: Coincident(g721,g722)
    c: Coincident(g961,g962)
    c: Coincident(g699,g700)
    c: Coincident(g944,g946)
    c: Coincident(g964,g965)
    c: Coincident(g720,g721)
    c: Coincident(g940,g941)
    c: Coincident(g714,g715)
    c: Coincident(g717,g718)
    c: Coincident(g698,g699)
    c: Coincident(g720,g730)
    c: Coincident(g941,g942)
    c: Coincident(g947,g949)
    c: Coincident(g960,g961)
    c: Coincident(g958,g965)
    c: Coincident(g718,g719)
    c: Coincident(g715,g716)
    c: Coincident(g943,g944)
    c: Coincident(g768,g769)
    c: Coincident(g769,g770)
    c: Coincident(g887,g888)
    c: Coincident(g886,g887)
    c: Coincident(g697,g698)
    c: Coincident(g959,g960)
    c: Coincident(g958,g959)
    c: Coincident(g763,g764)
    c: Coincident(g716,g717)
    c: Coincident(g882,g883)
    c: Coincident(g762,g763)
    c: Coincident(g883,g884)
    c: Coincident(g945,g947)
    c: Coincident(g767,g768)
    c: Coincident(g888,g889)
    c: Coincident(g885,g886)
    c: Coincident(g943,g945)
    c: Coincident(g911,g912)
    c: Coincident(g770,g771)
    c: Coincident(g764,g765)
    c: Coincident(g696,g697)
    c: Coincident(g881,g882)
    c: Coincident(g884,g885)
    c: Coincident(g761,g762)
    c: Coincident(g24,g25)
    c: Coincident(g32,g33)
    c: Coincident(g744,g745)
    c: Coincident(g745,g746)
    c: Coincident(g696,g719)
    c: Coincident(g25,g26)
    c: Coincident(g32,g35)
    c: Coincident(g771,g772)
    c: Coincident(g914,g915)
    c: Coincident(g765,g766)
    c: Coincident(g880,g881)
    c: Coincident(g760,g761)
    c: Coincident(g912,g913)
    c: Coincident(g739,g740)
    c: Coincident(g738,g739)
    c: Coincident(g766,g767)
    c: Coincident(g889,g890)
    c: Coincident(g743,g744)
    c: Coincident(g746,g747)
    c: Coincident(g879,g880)
    c: Coincident(g740,g741)
    c: Coincident(g772,g773)
    c: Coincident(g759,g760)
    c: Coincident(g913,g914)
    c: Coincident(g737,g738)
    c: Coincident(g890,g891)
    c: Coincident(g878,g879)
    c: Coincident(g747,g748)
    c: Coincident(g28,g29)
    c: Coincident(g29,g30)
    c: Coincident(g877,g878)
    c: Coincident(g891,g892)
    c: Coincident(g758,g759)
    c: Coincident(g741,g742)
    c: Coincident(g736,g737)
    c: Coincident(g742,g743)
    c: Coincident(g876,g877)
    c: Coincident(g916,g917)
    c: Coincident(g915,g916)
    c: Coincident(g37,g38)
    c: Coincident(g20,g23)
    c: Coincident(g845,g846)
    c: Coincident(g824,g825)
    c: Coincident(g773,g774)
    c: Coincident(g892,g893)
    c: Coincident(g748,g749)
    c: Coincident(g735,g736)
    c: Coincident(g910,g911)
    c: Coincident(g757,g758)
    c: Coincident(g875,g876)
    c: Coincident(g908,g909)
    c: Coincident(g825,g826)
    c: Coincident(g844,g845)
    c: Coincident(g907,g908)
    c: Coincident(g909,g910)
    c: Coincident(g792,g793)
    c: Coincident(g22,g23)
    c: Coincident(g38,g39)
    c: Coincident(g823,g824)
    c: Coincident(g846,g847)
    c: Coincident(g893,g894)
    c: Coincident(g865,g866)
    c: Coincident(g840,g841)
    c: Coincident(g819,g820)
    c: Coincident(g863,g865)
    c: Coincident(g917,g918)
    c: Coincident(g793,g794)
    c: Coincident(g776,g777)
    c: Coincident(g841,g842)
    c: Coincident(g818,g819)
    c: Coincident(g734,g735)
    c: Coincident(g874,g875)
    c: Coincident(g906,g907)
    c: Coincident(g820,g821)
    c: Coincident(g839,g840)
    c: Coincident(g774,g775)
    c: Coincident(g791,g792)
    c: Coincident(g894,g895)
    c: Coincident(g756,g757)
    c: Coincident(g787,g788)
    c: Coincident(g786,g787)
    c: Coincident(g843,g844)
    c: Coincident(g826,g827)
    c: Coincident(g777,g778)
    c: Coincident(g874,g897)
    c: Coincident(g788,g789)
    c: Coincident(g867,g873)
    c: Coincident(g749,g750)
    c: Coincident(g842,g843)
    c: Coincident(g901,g902)
    c: Coincident(g817,g818)
    c: Coincident(g733,g734)
    c: Coincident(g902,g903)
    c: Coincident(g872,g873)
    c: Coincident(g775,g776)
    c: Coincident(g821,g822)
    c: Coincident(g822,g823)
    c: Coincident(g838,g839)
    c: Coincident(g847,g848)
    c: Coincident(g794,g795)
    c: Coincident(g905,g906)
    c: Coincident(g871,g872)
    c: Coincident(g895,g896)
    c: Coincident(g785,g786)
    c: Coincident(g755,g756)
    c: Coincident(g898,g918)
    c: Coincident(g752,g753)
    c: Coincident(g789,g790)
    c: Coincident(g790,g791)
    c: Coincident(g816,g817)
    c: Coincident(g827,g828)
    c: Coincident(g837,g838)
    c: Coincident(g750,g751)
    c: Coincident(g732,g733)
    c: Coincident(g848,g849)
    c: Coincident(g755,g778)
    c: Coincident(g896,g897)
    c: Coincident(g795,g796)
    c: Coincident(g784,g785)
    c: Coincident(g815,g816)
    c: Coincident(g900,g901)
    c: Coincident(g814,g815)
    c: Coincident(g904,g905)
    c: Coincident(g753,g754)
    c: Coincident(g903,g904)
    c: Coincident(g836,g837)
    c: Coincident(g828,g829)
    c: Coincident(g829,g830)
    c: Coincident(g751,g752)
    c: Coincident(g849,g850)
    c: Coincident(g783,g784)
    c: Coincident(g830,g831)
    c: Coincident(g796,g797)
    c: Coincident(g812,g813)
    c: Coincident(g835,g836)
    c: Coincident(g898,g899)
    c: Coincident(g813,g814)
    c: Coincident(g731,g732)
    c: Coincident(g899,g900)
    c: Coincident(g811,g812)
    c: Coincident(g782,g783)
    c: Coincident(g834,g835)
    c: Coincident(g731,g754)
    c: Coincident(g870,g871)
    c: Coincident(g850,g851)
    c: Coincident(g803,g831)
    c: Coincident(g810,g811)
    c: Coincident(g869,g870)
    c: Coincident(g864,g866)
    c: Coincident(g868,g869)
    c: Coincident(g833,g834)
    c: Coincident(g781,g782)
    c: Coincident(g797,g798)
    c: Coincident(g807,g808)
    c: Coincident(g867,g868)
    c: Coincident(g861,g863)
    c: Coincident(g851,g852)
    c: Coincident(g806,g807)
    c: Coincident(g859,g861)
    c: Coincident(g862,g864)
    c: Coincident(g809,g810)
    c: Coincident(g860,g862)
    c: Coincident(g780,g781)
    c: Coincident(g852,g853)
    c: Coincident(g856,g857)
    c: Coincident(g832,g833)
    c: Coincident(g798,g799)
    c: Coincident(g857,g859)
    c: Coincident(g24,g27)
    c: Coincident(g33,g34)
    c: Coincident(g808,g809)
    c: Coincident(g803,g804)
    c: Coincident(g853,g854)
    c: Coincident(g800,g801)
    c: Coincident(g26,g27)
    c: Coincident(g34,g35)
    c: Coincident(g832,g855)
    c: Coincident(g805,g806)
    c: Coincident(g799,g800)
    c: Coincident(g804,g805)
    c: Coincident(g779,g780)
    c: Coincident(g854,g855)
    c: Coincident(g801,g802)
    c: Coincident(g858,g860)
    c: Coincident(g856,g858)
    c: Coincident(g779,g802)
    c: Coincident(g28,g31)
    c: Coincident(g30,g31)
FEATURE [PartDesign::Pad] Pad007
  BaseFeature = -> Fillet011
  Direction = (0,0,-1)
  Length = 1.5
  Length2 = 10
  Profile = -> Sketch023
  ReferenceAxis = -> Sketch023 [N_Axis]
  Refine = true
  Suppressed = false
  Type = 0
  expr: Length = 1.5
FEATURE [PartDesign::Body] Body022  label="desc_upper_ring"
  AllowCompound = false
  Group = -> [Sketch021,Pad006,Sketch022,Pocket006,PolarPattern005,Fillet010,Fillet011,Sketch023,Pad007]
  Origin = -> Origin036
  Tip = -> Pad007
COMPONENT P4 — recipe-attached ("motor_gear", modeled in this document).
Construction recipe (the document's own serialized feature program — sketch geometry with constraints, then the solid features built on it; lengths are millimeters unless a unit is written):

FEATURE [PartDesign::FeaturePython] InvoluteGear001  # WARN: FeaturePython — macro-defined, semantics opaque (R4)
  AttacherType = Attacher::AttachEngine3D
  Suppressed = false
  addendum_diameter = 27
  angular_backlash = 0
  axle_hole = false
  axle_holesize = 10
  backlash = 0
  clearance = 0.25
  double_helix = false
  head = 0
  head_fillet = 0
  height = 5
  helix_angle = 0
  module = 1.5
  num_teeth = 16
  numpoints = 20
  offset_hole = false
  offset_holeoffset = 10
  offset_holesize = 10
  pitch_diameter = 24
  pressure_angle = 20
  properties_from_tool = false
  reversed_backlash = false
  root_diameter = 20.25
  root_fillet = 0
  shift = 0
  simple = false
  transverse_pitch = 4.71239
  traverse_module = 1.5
  undercut = false
  version = 1.3.0
  expr: angular_backlash = backlash / pitch_diameter * 360 ° / pi
  expr: module = 1.5
  expr: num_teeth = 16
FEATURE [Sketcher::SketchObject] Sketch008
  ArcFitTolerance = 1e-06
  AttachmentSupport = -> [InvoluteGear001]
  FullyConstrained = true
  MakeInternals = false
  MapMode = 5
  Placement = pos=(0,0,5) rot=(0,0,1;0rad)
  expr: Constraints[11] = 3.1
  sketch-geometry (4):
    g0: ArcOfCircle CenterX=0 CenterY=0 CenterZ=0 NormalX=0 NormalY=0 NormalZ=1 AngleXU=0 Radius=2.5 StartAngle=2.47285 EndAngle=3.81034
    g1: ArcOfCircle CenterX=0 CenterY=0 CenterZ=0 NormalX=0 NormalY=0 NormalZ=1 AngleXU=0 Radius=2.5 StartAngle=5.61444 EndAngle=6.95193
    g2: LineSegment StartX=-1.9615 StartY=1.55 StartZ=0 EndX=1.9615 EndY=1.55 EndZ=0
    g3: LineSegment StartX=1.9615 StartY=-1.55 StartZ=0 EndX=-1.9615 EndY=-1.55 EndZ=0
  constraints (12):
    c: Coincident(g0,g-1)
    c: Coincident(g0,g1)
    c: Diameter(g0) = 5
    c: Equal(g1,g0)
    c: Coincident(g2,g0)
    c: Coincident(g2,g1)
    c: Coincident(g3,g1)
    c: Coincident(g3,g0)
    c: Parallel(g3,g2)
    c: Parallel(g-1,g2)
    c: Equal(g2,g3)
    c: Distance(g3,g2) = 3.1
FEATURE [PartDesign::Pocket] Pocket004
  BaseFeature = -> InvoluteGear001
  Direction = (0,0,-1)
  Length = 5
  Length2 = 5
  Profile = -> Sketch008
  ReferenceAxis = -> Sketch008 [N_Axis]
  Refine = true
  Suppressed = false
  Type = 0
FEATURE [PartDesign::Fillet] Fillet012
  Base = -> Pocket004 [Face5,Face4]
  BaseFeature = -> Pocket004
  Radius = 0.25
  Refine = true
  SupportTransform = false
  Suppressed = false
  UseAllEdges = false
  expr: Radius = 0.25
FEATURE [PartDesign::Body] Body005  label="motor_gear001"
  AllowCompound = false
  Group = -> [InvoluteGear001,Sketch008,Pocket004,Fillet012]
  Origin = -> Origin010
  Placement = pos=(0,0,75) rot=(0,0,1;0rad)
  Tip = -> Fillet012
COMPONENT P5 — recipe-attached ("pill_sections", modeled in this document).
Construction recipe (the document's own serialized feature program — sketch geometry with constraints, then the solid features built on it; lengths are millimeters unless a unit is written):

FEATURE [PartDesign::FeaturePython] InternalInvoluteGear  # WARN: FeaturePython — macro-defined, semantics opaque (R4)
  AttacherType = Attacher::AttachEngine3D
  Suppressed = false
  addendum_diameter = 94.2
  angular_backlash = 0
  backlash = 0
  clearance = 0.2
  double_helix = false
  head = -0.4
  head_fillet = 0
  height = 5
  helix_angle = 0
  module = 1.5
  num_teeth = 64
  numpoints = 20
  outside_diameter = 106
  pitch_diameter = 96
  pressure_angle = 20
  properties_from_tool = false
  reversed_backlash = false
  root_diameter = 99.6
  root_fillet = 0
  shift = 0
  simple = false
  thickness = 5
  transverse_pitch = 4.71239
  version = 1.3.0
  expr: angular_backlash = backlash / pitch_diameter * 360 ° / pi
  expr: clearance = 0.2
  expr: module = 1.5
  expr: num_teeth = 64
  expr: pressure_angle = 20
FEATURE [Sketcher::SketchObject] Sketch010
  ArcFitTolerance = 1e-06
  ExternalGeometry = -> [InternalInvoluteGear]
  FullyConstrained = false
  MakeInternals = false
  MapMode = 5
  Placement = pos=(53,0,0) rot=(1,0,0;1.5708rad)
  expr: Constraints[10] = VarSet.outer_wall_thickness
  expr: Constraints[11] = VarSet.outer_wall_thickness
  expr: Constraints[14] = VarSet.outer_wall_thickness
  expr: Constraints[17] = VarSet.fillet_oouter_gear
  expr: Constraints[2] = 5
  expr: Constraints[34] = VarSet.outer_wall_thickness
  expr: Constraints[36] = VarSet.outer_ring_height
  expr: Constraints[37] = VarSet.fillet_oouter_gear
  expr: Constraints[38] = 30
  expr: Constraints[45] = VarSet.fillet_oouter_gear
  expr: Constraints[50] = 25
  expr: Constraints[52] = 10
  expr: Constraints[6] = 25
  expr: Constraints[9] = VarSet.outer_wall_thickness
  sketch-geometry (28):
    g0: LineSegment StartX=0 StartY=0 StartZ=0 EndX=0 EndY=5 EndZ=0
    g1: LineSegment StartX=0 StartY=0 StartZ=0 EndX=24.0192 EndY=0 EndZ=0
    g2: LineSegment StartX=25.6005 StartY=0.775418 StartZ=0 EndX=40.7862 EndY=20.3842 EndZ=0
    g3: LineSegment StartX=24.6198 StartY=2.77542 StartZ=0 EndX=39.2049 EndY=21.6088 EndZ=0
    g4: LineSegment StartX=9.57963 StartY=2 StartZ=0 EndX=23.0385 EndY=2 EndZ=0
    g5: LineSegment StartX=0 StartY=5 StartZ=0 EndX=-2 EndY=5 EndZ=0
    g6: LineSegment StartX=-0.122418 StartY=35.2036 StartZ=0 EndX=4.22e-14 EndY=7.67973 EndZ=0
    g7: LineSegment StartX=8.57963 StartY=2.26795 StartZ=0 EndX=0.399992 EndY=6.99046 EndZ=0
    g8: ArcOfCircle CenterX=0.799992 CenterY=7.68328 CenterZ=0 NormalX=0 NormalY=0 NormalZ=1 AngleXU=0 Radius=0.8 StartAngle=3.14604 EndAngle=4.18879
    g9: ArcOfCircle CenterX=9.57963 CenterY=4 CenterZ=0 NormalX=0 NormalY=0 NormalZ=1 AngleXU=0 Radius=2 StartAngle=4.18879 EndAngle=4.71239
    g10: GeomPoint [constr] X=9.04373 Y=2 Z=0
    g11: ArcOfCircle CenterX=23.0385 CenterY=4 CenterZ=0 NormalX=0 NormalY=0 NormalZ=1 AngleXU=0 Radius=2 StartAngle=4.71239 EndAngle=5.62423
    g12: GeomPoint [constr] X=24.0192 Y=2 Z=0
    g13: ArcOfCircle CenterX=24.0192 CenterY=2 CenterZ=0 NormalX=0 NormalY=0 NormalZ=1 AngleXU=0 Radius=2 StartAngle=4.71239 EndAngle=5.62423
    g14: GeomPoint [constr] X=25 Y=0 Z=0
    g15: GeomPoint [constr] X=29 Y=5.16508 Z=0
    g16: GeomPoint [constr] X=27 Y=5.84896 Z=0
    g17: ArcOfCircle CenterX=-0.92241 CenterY=35.2 CenterZ=0 NormalX=0 NormalY=0 NormalZ=1 AngleXU=0 Radius=0.8 StartAngle=0.00444768 EndAngle=1.5708
    g18: LineSegment StartX=-10.9224 StartY=36 StartZ=0 EndX=-5.92241 EndY=36 EndZ=0
    g19: ArcOfCircle CenterX=19.4391 CenterY=36.916 CenterZ=0 NormalX=0 NormalY=0 NormalZ=1 AngleXU=0 Radius=27 StartAngle=5.62423 EndAngle=6.21764
    g20: ArcOfCircle CenterX=19.4391 CenterY=36.916 CenterZ=0 NormalX=0 NormalY=0 NormalZ=1 AngleXU=0 Radius=25 StartAngle=5.62423 EndAngle=6.21662
    g21: ArcOfCircle CenterX=45.1819 CenterY=35.2 CenterZ=0 NormalX=0 NormalY=0 NormalZ=1 AngleXU=0 Radius=0.8 StartAngle=1.5708 EndAngle=3.07503
    g22: LineSegment StartX=45.5828 StartY=36 StartZ=0 EndX=45.1819 EndY=36 EndZ=0
    g23: ArcOfCircle CenterX=45.5828 CenterY=35.2 CenterZ=0 NormalX=0 NormalY=0 NormalZ=1 AngleXU=0 Radius=0.8 StartAngle=6.21764 EndAngle=7.85398
    g24: ArcOfCircle CenterX=-10.9224 CenterY=35.2 CenterZ=0 NormalX=0 NormalY=0 NormalZ=1 AngleXU=0 Radius=0.8 StartAngle=1.5708 EndAngle=3.66964
    g25: LineSegment StartX=-11.6134 StartY=34.7969 StartZ=0 EndX=-2.05968 EndY=18.418 EndZ=0
    g26: LineSegment StartX=-2.05968 StartY=18.418 StartZ=0 EndX=-2 EndY=5 EndZ=0
    g27: LineSegment StartX=-5.92241 StartY=36 StartZ=0 EndX=-0.92241 EndY=36 EndZ=0
  constraints (66):
    c: Coincident(g0,g-1)
    c: PointOnObject(g0,g-2)
    c: DistanceY(g0,g0) = 5
    c: Coincident(g1,g0)
    c: PointOnObject(g14,g-1)
    c: Parallel(g3,g2)
    c: DistanceX(g1,g14) = 25
    c: DistanceX(g14,g15) = 4
    c: Parallel(g4,g1)
    c: Distance(g1,g4) = 2
    c: DistanceX(g16,g15) = 2
    c: Distance(g14,g3) = 2
    c: Coincident(g5,g0)
    c: Horizontal(g5)
    c: DistanceX(g5,g5) = 2
    c: Tangent(g8,g7) = 1.5708
    c: Tangent(g8,g6) = -1.5708
    c: Radius(g8) = 0.8
    c: PointOnObject(g6,g-2)
    c: PointOnObject(g10,g7)
    c: PointOnObject(g10,g4)
    c: Tangent(g7,g9) = 1.5708
    c: Tangent(g4,g9) = -1.5708
    c: PointOnObject(g12,g4)
    c: PointOnObject(g12,g3)
    c: Tangent(g4,g11) = -1.5708
    c: Tangent(g3,g11) = -1.5708
    c: PointOnObject(g14,g1)
    c: PointOnObject(g14,g2)
    c: Tangent(g1,g13) = -1.5708
    c: Tangent(g2,g13) = -1.5708
    c: PointOnObject(g15,g2)
    c: PointOnObject(g16,g3)
    c: Equal(g13,g11)
    c: Distance(g0,g8) = 2
    c: Tangent(g17,g6) = 1.5708
    c: Distance(g18,g-1) = 36
    c: Radius(g17) = 0.8
    c: Angle(g7,g1) = 0.523599
    c: Equal(g11,g9)
    c: Coincident(g20,g19)
    c: Tangent(g20,g3) = -1.5708
    c: Tangent(g19,g2) = -1.5708
    c: Tangent(g22,g21) = -1.5708
    c: Tangent(g21,g20) = 1.5708
    c: Radius(g21) = 0.8
    c: Tangent(g23,g22) = -1.5708
    c: Tangent(g23,g19) = -1.5708
    c: Equal(g23,g21)
    c: Parallel(g22,g-1)
    c: Radius(g20) = 25
    c: Radius(g11) = 2
    c: DistanceX(g18,g27) = 10
    c: Tangent(g24,g18) = 1.5708
    c: Equal(g24,g17)
    c: Coincident(g26,g25)
    c: Coincident(g26,g5)
    c: Parallel(g26,g6)
    c: Tangent(g25,g24) = -1.5708
    c: Perpendicular(g-2,g18)
    c: Perpendicular(g-2,g27)
    c: Coincident(g18,g27)
    c: Tangent(g27,g17) = 1.5708
    c: Equal(g27,g18)
    c: Angle(g26,g25) = 0.523599
    c: Vertical(g18,g-3)
FEATURE [PartDesign::Revolution] Revolution001
  Angle = 360
  Angle2 = 60
  Axis = (1e-16,1e-16,1)
  Base = (0,0,0)
  BaseFeature = -> InternalInvoluteGear
  Profile = -> Sketch010
  ReferenceAxis = -> Z_Axis013
  Refine = true
  Reversed = true
  Suppressed = false
  Type = 0
FEATURE [Sketcher::SketchObject] Sketch011
  ArcFitTolerance = 1e-06
  ExternalGeometry = -> [Revolution001]
  FullyConstrained = true
  MakeInternals = false
  MapMode = 5
  Placement = pos=(53,0,0) rot=(1,0,0;1.5708rad)
  sketch-geometry (2):
    g0: LineSegment StartX=-0.92241 StartY=36 StartZ=0 EndX=45.1819 EndY=36 EndZ=0
    g1: LineSegment StartX=9.57963 StartY=2 StartZ=0 EndX=23.0385 EndY=2 EndZ=0
  constraints (4):
    c: Coincident(g0,g-11)
    c: Coincident(g0,g-7)
    c: Tangent(g1,g-6) = -1.5708
    c: Coincident(g1,g-8)
FEATURE [PartDesign::Revolution] Revolution002
  Angle = 1
  Angle2 = 60
  Axis = (1e-16,1e-16,1)
  Base = (0,0,0)
  BaseFeature = -> Revolution001
  Midplane = true
  Profile = -> Sketch011
  ReferenceAxis = -> Z_Axis013
  Refine = true
  Suppressed = false
  Type = 0
  expr: Angle = 1
FEATURE [PartDesign::PolarPattern] PolarPattern
  Angle = 360
  Axis = -> Z_Axis013
  BaseFeature = -> Revolution002
  Mode = 0
  Occurrences = 32
  Offset = 120
  Originals = -> [Revolution002]
  Refine = true
  Suppressed = false
  TransformMode = 0
  expr: Occurrences = 32
FEATURE [Sketcher::SketchObject] Sketch015
  ArcFitTolerance = 1e-06
  AttachmentSupport = -> [PolarPattern]
  ExternalGeometry = -> [PolarPattern]
  FullyConstrained = true
  MakeInternals = false
  MapMode = 5
  Placement = pos=(4e-15,4e-15,36) rot=(0,0,1;0rad)
  expr: Constraints[13] = 9
  sketch-geometry (5):
    g0: Circle [constr] CenterX=0 CenterY=0 CenterZ=0 NormalX=0 NormalY=0 NormalZ=1 AngleXU=0 Radius=52.0776
    g1: Circle CenterX=0 CenterY=0 CenterZ=0 NormalX=0 NormalY=0 NormalZ=1 AngleXU=0 Radius=42.5776
    g2: Circle CenterX=0 CenterY=0 CenterZ=0 NormalX=0 NormalY=0 NormalZ=1 AngleXU=0 Radius=51.5776
    g3: LineSegment [constr] StartX=-42.5776 StartY=0 StartZ=0 EndX=-42.0776 EndY=0 EndZ=0
    g4: LineSegment [constr] StartX=-52.0776 StartY=0 StartZ=0 EndX=-51.5776 EndY=0 EndZ=0
  constraints (14):
    c: Coincident(g0,g-3)
    c: PointOnObject(g-4,g0)
    c: Coincident(g1,g0)
    c: Coincident(g2,g0)
    c: PointOnObject(g3,g1)
    c: PointOnObject(g3,g-3)
    c: PointOnObject(g3,g-1)
    c: PointOnObject(g3,g-1)
    c: PointOnObject(g4,g0)
    c: PointOnObject(g4,g2)
    c: PointOnObject(g4,g-1)
    c: PointOnObject(g4,g-1)
    c: Equal(g4,g3)
    c: Distance(g2,g1) = 9
FEATURE [PartDesign::Pocket] Pocket005
  BaseFeature = -> PolarPattern
  Direction = (0,0,-1)
  Length = 3
  Length2 = 5
  Profile = -> Sketch015
  ReferenceAxis = -> Sketch015 [N_Axis]
  Refine = true
  Suppressed = false
  Type = 0
  expr: Length = 3
FEATURE [PartDesign::Fillet] Fillet003
  Base = -> Pocket005 [Edge312,Edge949]
  BaseFeature = -> Pocket005
  Radius = 1
  Refine = true
  SupportTransform = false
  Suppressed = false
  UseAllEdges = false
  expr: Radius = 1
FEATURE [Sketcher::SketchObject] Sketch016
  ArcFitTolerance = 1e-06
  AttachmentSupport = -> [Fillet003]
  ExternalGeometry = -> [Fillet003]
  FullyConstrained = false
  MakeInternals = false
  MapMode = 5
  Placement = pos=(0,0,33) rot=(0,0,1;0rad)
  sketch-geometry (8):
    g0: ArcOfCircle CenterX=4e-15 CenterY=4e-15 CenterZ=0 NormalX=0 NormalY=0 NormalZ=1 AngleXU=0 Radius=44.0776 StartAngle=1.01451 EndAngle=1.42895
    g1: ArcOfCircle CenterX=4e-15 CenterY=4e-15 CenterZ=0 NormalX=0 NormalY=0 NormalZ=1 AngleXU=0 Radius=50.0776 StartAngle=1.01451 EndAngle=1.42895
    g2: LineSegment StartX=6.23147 StartY=43.6349 StartZ=0 EndX=7.07972 EndY=49.5746 EndZ=0
    g3: LineSegment StartX=23.2744 StartY=37.4318 StartZ=0 EndX=26.4426 EndY=42.5271 EndZ=0
    g4: LineSegment [constr] StartX=23.2744 StartY=37.4318 StartZ=0 EndX=23.0104 EndY=37.0071 EndZ=0
    g5: LineSegment [constr] StartX=26.4426 StartY=42.5271 StartZ=0 EndX=26.7066 EndY=42.9517 EndZ=0
    g6: LineSegment [constr] StartX=4e-15 StartY=4e-15 StartZ=0 EndX=-40.9495 EndY=14.9044 EndZ=0
    g7: LineSegment [constr] StartX=4e-15 StartY=4e-15 StartZ=0 EndX=14.9044 EndY=40.9495 EndZ=0
  constraints (22):
    c: Coincident(g0,g-4)
    c: Coincident(g1,g0)
    c: Coincident(g2,g0)
    c: Coincident(g2,g1)
    c: Coincident(g3,g0)
    c: Coincident(g3,g1)
    c: Equal(g2,g3)
    c: Perpendicular(g0,g2)
    c: Coincident(g4,g0)
    c: PointOnObject(g4,g-4)
    c: Coincident(g5,g1)
    c: PointOnObject(g5,g-3)
    c: Parallel(g4,g3)
    c: Parallel(g3,g5)
    c: Equal(g5,g4)
    c: Distance(g3,g3) = 6
    c: Coincident(g6,g0)
    c: Angle(g6,g-1) = 0.349066
    c: PointOnObject(g6,g-4)
    c: Coincident(g7,g0)
    c: Perpendicular(g6,g7)
    c: Equal(g7,g6)
FEATURE [PartDesign::Pad] Pad004
  BaseFeature = -> Fillet003
  Direction = (0,0,1)
  Length = 1.5
  Length2 = 10
  Profile = -> Sketch016
  ReferenceAxis = -> Sketch016 [N_Axis]
  Refine = true
  Suppressed = false
  Type = 0
  expr: Length = 1.5
FEATURE [PartDesign::PolarPattern] PolarPattern002
  Angle = 360
  Axis = -> Sketch016 [N_Axis]
  BaseFeature = -> Pad004
  Mode = 0
  Occurrences = 2
  Offset = 120
  Originals = -> [Pad004]
  Refine = true
  Suppressed = false
  TransformMode = 0
FEATURE [PartDesign::Fillet] Fillet004
  Base = -> PolarPattern002 [Face177,Face175]
  BaseFeature = -> PolarPattern002
  Radius = 1
  Refine = true
  SupportTransform = false
  Suppressed = false
  UseAllEdges = false
FEATURE [PartDesign::Body] Body016  label="outer_gear"
  AllowCompound = false
  Group = -> [InternalInvoluteGear,Sketch010,Revolution001,Sketch011,Revolution002,PolarPattern,Sketch015,Pocket005,Fillet003,Sketch016,Pad004,PolarPattern002,Fillet004]
  Origin = -> Origin026
  Placement = pos=(0,0,41) rot=(0,0,1;0rad)
  Tip = -> Fillet004
COMPONENT P6 — recipe-attached ("upper_cover_display", modeled in this document).
Construction recipe (the document's own serialized feature program — sketch geometry with constraints, then the solid features built on it; lengths are millimeters unless a unit is written):

FEATURE [Sketcher::SketchObject] Sketch012
  ArcFitTolerance = 1e-06
  AttachmentSupport = -> [Origin034]
  FullyConstrained = true
  MakeInternals = false
  MapMode = 5
  expr: Constraints[2] = 80
  sketch-geometry (3):
    g0: Circle CenterX=0 CenterY=0 CenterZ=0 NormalX=0 NormalY=0 NormalZ=1 AngleXU=0 Radius=21
    g1: Circle CenterX=0 CenterY=0 CenterZ=0 NormalX=0 NormalY=0 NormalZ=1 AngleXU=0 Radius=40
    g2: Circle CenterX=0 CenterY=0 CenterZ=0 NormalX=0 NormalY=0 NormalZ=1 AngleXU=0 Radius=38.5
  constraints (6):
    c: Diameter(g0) = 42
    c: Coincident(g0,g-1)
    c: Diameter(g1) = 80
    c: Coincident(g1,g0)
    c: Coincident(g2,g0)
    c: Diameter(g2) = 77
FEATURE [PartDesign::Pad] Pad005
  Direction = (0,0,1)
  Length = 3
  Length2 = 10
  Profile = -> Sketch012 [Edge2,Edge1]
  ReferenceAxis = -> Sketch012 [N_Axis]
  Refine = true
  Suppressed = false
  Type = 0
  expr: Length = 3
FEATURE [Sketcher::SketchObject] Sketch017
  ArcFitTolerance = 1e-06
  FullyConstrained = true
  MakeInternals = false
  MapMode = 5
  Placement = pos=(40,0,0) rot=(1,0,0;1.5708rad)
  expr: Constraints[4] = 14
  sketch-geometry (6):
    g0: LineSegment StartX=5.78797 StartY=-27 StartZ=0 EndX=5.78797 EndY=-13 EndZ=0
    g1: LineSegment StartX=5.78797 StartY=-13 StartZ=0 EndX=0 EndY=0 EndZ=0
    g2: LineSegment StartX=0 StartY=0 StartZ=0 EndX=-1.5 EndY=0 EndZ=0
    g3: LineSegment StartX=-1.5 StartY=0 StartZ=0 EndX=4.28797 EndY=-13 EndZ=0
    g4: LineSegment StartX=4.28797 StartY=-13 StartZ=0 EndX=4.28797 EndY=-27 EndZ=0
    g5: LineSegment StartX=4.28797 StartY=-27 StartZ=0 EndX=5.78797 EndY=-27 EndZ=0
  constraints (17):
    c: Vertical(g0)
    c: Coincident(g1,g0)
    c: Coincident(g1,g-1)
    c: Angle(g0,g1) = 0.418879
    c: DistanceY(g0,g0) = 14
    c: DistanceY(g0,g1) = 27
    c: Coincident(g2,g1)
    c: PointOnObject(g2,g-1)
    c: Coincident(g2,g3)
    c: Coincident(g3,g4)
    c: Vertical(g4)
    c: Coincident(g4,g5)
    c: Coincident(g5,g0)
    c: Perpendicular(g4,g5)
    c: Equal(g3,g1)
    c: Parallel(g3,g1)
    c: DistanceX(g5,g5) = 1.5
FEATURE [PartDesign::Revolution] Revolution003
  Angle = 360
  Angle2 = 60
  Axis = (1e-16,1e-16,1)
  Base = (0,0,0)
  BaseFeature = -> Pad005
  Profile = -> Sketch017
  ReferenceAxis = -> Z_Axis017
  Refine = true
  Reversed = true
  Suppressed = false
  Type = 0
FEATURE [PartDesign::Chamfer] Chamfer
  Angle = 45
  Base = -> Revolution003 [Edge13,Edge10]
  BaseFeature = -> Revolution003
  ChamferType = 0
  FlipDirection = false
  Refine = true
  Size = 2
  Size2 = 1
  SupportTransform = false
  Suppressed = false
  UseAllEdges = false
FEATURE [Sketcher::SketchObject] Sketch018
  ArcFitTolerance = 1e-06
  FullyConstrained = true
  MakeInternals = false
  MapMode = 5
  Placement = pos=(44.288,-6.1e-15,-27) rot=(0,0.707107,0.707107;3.14159rad)
  sketch-geometry (4):
    g0: LineSegment StartX=0 StartY=0 StartZ=0 EndX=0 EndY=5.12132 EndZ=0
    g1: LineSegment StartX=0 StartY=5.12132 StartZ=0 EndX=2.12132 EndY=3 EndZ=0
    g2: LineSegment StartX=2.12132 StartY=3 StartZ=0 EndX=2.12132 EndY=0 EndZ=0
    g3: LineSegment StartX=2.12132 StartY=0 StartZ=0 EndX=0 EndY=0 EndZ=0
  constraints (11):
    c: Coincident(g-1,g0)
    c: Vertical(g0)
    c: Coincident(g0,g1)
    c: Coincident(g1,g2)
    c: PointOnObject(g2,g-1)
    c: Vertical(g2)
    c: Coincident(g2,g3)
    c: Coincident(g3,g0)
    c: Angle(g2,g1) = 0.785398
    c: Equal(g2,g1)
    c: DistanceY(g2,g2) = 3
FEATURE [PartDesign::Revolution] Revolution004
  Angle = 9
  Angle2 = 60
  Axis = (1e-16,1e-16,1)
  Base = (0,0,0)
  BaseFeature = -> Chamfer
  Profile = -> Sketch018
  ReferenceAxis = -> Z_Axis017
  Refine = true
  Suppressed = false
  Type = 0
  expr: Angle = 9
FEATURE [PartDesign::PolarPattern] PolarPattern003
  Angle = 360
  Axis = -> Z_Axis017
  BaseFeature = -> Revolution004
  Mode = 0
  Occurrences = 4
  Offset = 120
  Originals = -> [Revolution004]
  Refine = true
  Suppressed = false
  TransformMode = 0
FEATURE [PartDesign::Fillet] Fillet009
  Base = -> PolarPattern003 [Face21,Face22,Face23,Face7]
  BaseFeature = -> PolarPattern003
  Radius = 0.5
  Refine = true
  SupportTransform = false
  Suppressed = false
  UseAllEdges = false
  expr: Radius = 0.5
FEATURE [PartDesign::Body] Body021  label="upper_cover_display"
  AllowCompound = false
  Group = -> [Sketch012,Pad005,Sketch017,Revolution003,Chamfer,Sketch018,Revolution004,PolarPattern003,Fillet009]
  Origin = -> Origin034
  Tip = -> Fillet009
PROVENANCE & LICENSES
A FreeCAD (.FCStd) document from a public repository crawl; recipes are the document's own serialized feature recipes (and, for linked parts, companion documents' recipes).
License: mit.
